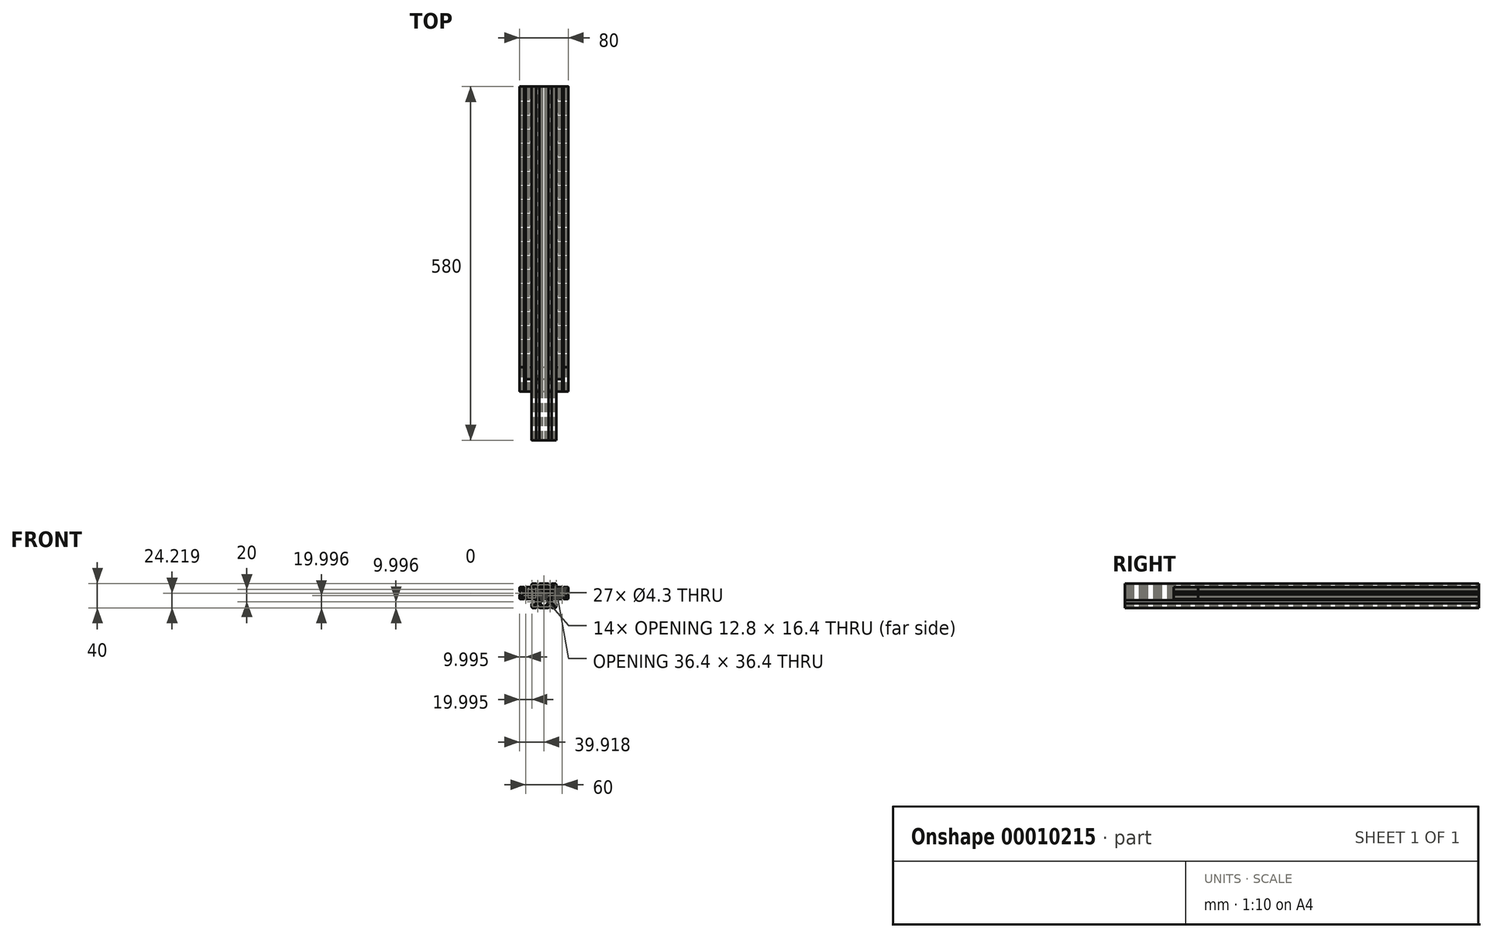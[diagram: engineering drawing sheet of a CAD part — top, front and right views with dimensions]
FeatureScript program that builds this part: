
annotation { "Feature Type Name" : "Feature", "Feature Type Description" : "" }
export const myFeature = defineFeature(function(context is Context, id is Id, definition is map)
    precondition{}
    {
        {
            var Q0;
            Q0=qCreatedBy(makeId("Front.planeOp"),FACE);
            var sketch = newSketch(context, id + "F0", { "sketchPlane" : qUnion([Q0])});
            skArc(sketch, "E0.0", {"start": v(-8.5, 10) * mm, "mid": v(-9.56, 9.56) * mm, "end": v(-10, 8.5) * mm});
            skLineSegment(sketch, "E1.0", {"start": v(-10, 8.5) * mm, "end": v(-10, 3) * mm});
            skArc(sketch, "E2.0", {"start": v(-2.5, 9.5) * mm, "mid": v(-2.65, 9.85) * mm, "end": v(-3, 10) * mm});
            skLineSegment(sketch, "E3.0", {"start": v(-2.5, 9.5) * mm, "end": v(-2.5, 8.45) * mm});
            skLineSegment(sketch, "E4.0", {"start": v(-2.75, 8.2) * mm, "end": v(-4.44, 8.2) * mm});
            skArc(sketch, "E5.0", {"start": v(-4.44, 8.2) * mm, "mid": v(-5.46, 7.52) * mm, "end": v(-5.22, 6.32) * mm});
            skLineSegment(sketch, "E6.0", {"start": v(-2.94, 4.04) * mm, "end": v(-5.22, 6.32) * mm});
            skArc(sketch, "E7.0", {"start": v(-2.94, 4.04) * mm, "mid": v(-2.45, 3.71) * mm, "end": v(-1.88, 3.6) * mm});
            skLineSegment(sketch, "E8.0", {"start": v(-1.88, 3.6) * mm, "end": v(1.88, 3.6) * mm});
            skArc(sketch, "E9.0", {"start": v(1.88, 3.6) * mm, "mid": v(2.45, 3.71) * mm, "end": v(2.94, 4.04) * mm});
            skLineSegment(sketch, "E10.0", {"start": v(2.94, 4.04) * mm, "end": v(5.22, 6.32) * mm});
            skArc(sketch, "E11.0", {"start": v(5.22, 6.32) * mm, "mid": v(5.46, 7.52) * mm, "end": v(4.44, 8.2) * mm});
            skLineSegment(sketch, "E12.0", {"start": v(4.44, 8.2) * mm, "end": v(2.75, 8.2) * mm});
            skArc(sketch, "E13.0", {"start": v(3, 10) * mm, "mid": v(2.65, 9.85) * mm, "end": v(2.5, 9.5) * mm});
            skLineSegment(sketch, "E14.0", {"start": v(3, 10) * mm, "end": v(8.5, 10) * mm});
            skArc(sketch, "E15.0", {"start": v(10, 8.5) * mm, "mid": v(9.56, 9.56) * mm, "end": v(8.5, 10) * mm});
            skLineSegment(sketch, "E16.0", {"start": v(10, 8.5) * mm, "end": v(10, 3) * mm});
            skArc(sketch, "E17.0", {"start": v(9.5, 2.5) * mm, "mid": v(9.85, 2.65) * mm, "end": v(10, 3) * mm});
            skLineSegment(sketch, "E18.0", {"start": v(8.45, 2.5) * mm, "end": v(9.5, 2.5) * mm});
            skLineSegment(sketch, "E19.0", {"start": v(-8.5, 10) * mm, "end": v(-3, 10) * mm});
            skArc(sketch, "E20.0", {"start": v(-10, 3) * mm, "mid": v(-9.85, 2.65) * mm, "end": v(-9.5, 2.5) * mm});
            skLineSegment(sketch, "E21.0", {"start": v(-8.45, 2.5) * mm, "end": v(-9.5, 2.5) * mm});
            skArc(sketch, "E22.0", {"start": v(-8.45, 2.5) * mm, "mid": v(-8.27, 2.57) * mm, "end": v(-8.2, 2.75) * mm});
            skLineSegment(sketch, "E22.1", {"start": v(-8.2, 4.44) * mm, "end": v(-8.2, 2.75) * mm});
            skArc(sketch, "E22.2", {"start": v(-6.32, 5.22) * mm, "mid": v(-7.52, 5.46) * mm, "end": v(-8.2, 4.44) * mm});
            skLineSegment(sketch, "E23.0", {"start": v(-4.04, 2.94) * mm, "end": v(-6.32, 5.22) * mm});
            skArc(sketch, "E24.0", {"start": v(-3.6, 1.88) * mm, "mid": v(-3.71, 2.45) * mm, "end": v(-4.04, 2.94) * mm});
            skLineSegment(sketch, "E25.0", {"start": v(-3.6, 1.88) * mm, "end": v(-3.6, -1.88) * mm});
            skArc(sketch, "E26.0", {"start": v(-4.04, -2.94) * mm, "mid": v(-3.71, -2.45) * mm, "end": v(-3.6, -1.88) * mm});
            skLineSegment(sketch, "E27.0", {"start": v(-4.04, -2.94) * mm, "end": v(-6.32, -5.22) * mm});
            skArc(sketch, "E28.0", {"start": v(-8.2, -4.44) * mm, "mid": v(-7.52, -5.46) * mm, "end": v(-6.32, -5.22) * mm});
            skLineSegment(sketch, "E29.0", {"start": v(-8.2, -2.75) * mm, "end": v(-8.2, -4.44) * mm});
            skArc(sketch, "E30.0", {"start": v(-8.2, -2.75) * mm, "mid": v(-8.27, -2.57) * mm, "end": v(-8.45, -2.5) * mm});
            skLineSegment(sketch, "E31.0", {"start": v(-8.45, -2.5) * mm, "end": v(-9.5, -2.5) * mm});
            skArc(sketch, "E32.0", {"start": v(-9.5, -2.5) * mm, "mid": v(-9.85, -2.65) * mm, "end": v(-10, -3) * mm});
            skLineSegment(sketch, "E33.0", {"start": v(-10, -3) * mm, "end": v(-10, -8.5) * mm});
            skArc(sketch, "E34.0", {"start": v(-10, -8.5) * mm, "mid": v(-9.56, -9.56) * mm, "end": v(-8.5, -10) * mm});
            skLineSegment(sketch, "E35.0", {"start": v(-8.5, -10) * mm, "end": v(-3, -10) * mm});
            skArc(sketch, "E36.0", {"start": v(-3, -10) * mm, "mid": v(-2.65, -9.85) * mm, "end": v(-2.5, -9.5) * mm});
            skLineSegment(sketch, "E37.0", {"start": v(-2.5, -9.5) * mm, "end": v(-2.5, -8.45) * mm});
            skArc(sketch, "E38.0", {"start": v(-2.5, -8.45) * mm, "mid": v(-2.57, -8.27) * mm, "end": v(-2.75, -8.2) * mm});
            skLineSegment(sketch, "E39.0", {"start": v(-4.44, -8.2) * mm, "end": v(-2.75, -8.2) * mm});
            skArc(sketch, "E40.0", {"start": v(-5.22, -6.32) * mm, "mid": v(-5.46, -7.52) * mm, "end": v(-4.44, -8.2) * mm});
            skLineSegment(sketch, "E41.0", {"start": v(-2.94, -4.04) * mm, "end": v(-5.22, -6.32) * mm});
            skArc(sketch, "E42.0", {"start": v(-1.88, -3.6) * mm, "mid": v(-2.45, -3.71) * mm, "end": v(-2.94, -4.04) * mm});
            skLineSegment(sketch, "E43.0", {"start": v(-1.88, -3.6) * mm, "end": v(1.88, -3.6) * mm});
            skArc(sketch, "E44.0", {"start": v(2.94, -4.04) * mm, "mid": v(2.45, -3.71) * mm, "end": v(1.88, -3.6) * mm});
            skLineSegment(sketch, "E45.0", {"start": v(2.94, -4.04) * mm, "end": v(5.22, -6.32) * mm});
            skArc(sketch, "E46.0", {"start": v(4.44, -8.2) * mm, "mid": v(5.46, -7.52) * mm, "end": v(5.22, -6.32) * mm});
            skLineSegment(sketch, "E47.0", {"start": v(2.75, -8.2) * mm, "end": v(4.44, -8.2) * mm});
            skArc(sketch, "E48.0", {"start": v(2.75, -8.2) * mm, "mid": v(2.57, -8.27) * mm, "end": v(2.5, -8.45) * mm});
            skLineSegment(sketch, "E49.0", {"start": v(2.5, -9.5) * mm, "end": v(2.5, -8.45) * mm});
            skArc(sketch, "E50.0", {"start": v(2.5, -9.5) * mm, "mid": v(2.65, -9.85) * mm, "end": v(3, -10) * mm});
            skLineSegment(sketch, "E51.0", {"start": v(3, -10) * mm, "end": v(8.5, -10) * mm});
            skArc(sketch, "E52.0", {"start": v(8.5, -10) * mm, "mid": v(9.56, -9.56) * mm, "end": v(10, -8.5) * mm});
            skLineSegment(sketch, "E53.0", {"start": v(10, -3) * mm, "end": v(10, -8.5) * mm});
            skArc(sketch, "E54.0", {"start": v(10, -3) * mm, "mid": v(9.85, -2.65) * mm, "end": v(9.5, -2.5) * mm});
            skLineSegment(sketch, "E55.0", {"start": v(8.45, -2.5) * mm, "end": v(9.5, -2.5) * mm});
            skArc(sketch, "E56.0", {"start": v(8.45, -2.5) * mm, "mid": v(8.27, -2.57) * mm, "end": v(8.2, -2.75) * mm});
            skLineSegment(sketch, "E57.0", {"start": v(8.2, -4.44) * mm, "end": v(8.2, -2.75) * mm});
            skArc(sketch, "E58.0", {"start": v(6.32, -5.22) * mm, "mid": v(7.52, -5.46) * mm, "end": v(8.2, -4.44) * mm});
            skLineSegment(sketch, "E59.0", {"start": v(4.04, -2.94) * mm, "end": v(6.32, -5.22) * mm});
            skArc(sketch, "E60.0", {"start": v(3.6, -1.88) * mm, "mid": v(3.71, -2.45) * mm, "end": v(4.04, -2.94) * mm});
            skLineSegment(sketch, "E61.0", {"start": v(3.6, 1.88) * mm, "end": v(3.6, -1.88) * mm});
            skArc(sketch, "E62.0", {"start": v(4.04, 2.94) * mm, "mid": v(3.71, 2.45) * mm, "end": v(3.6, 1.88) * mm});
            skLineSegment(sketch, "E63.0", {"start": v(4.04, 2.94) * mm, "end": v(6.32, 5.22) * mm});
            skArc(sketch, "E64.0", {"start": v(8.2, 4.44) * mm, "mid": v(7.52, 5.46) * mm, "end": v(6.32, 5.22) * mm});
            skLineSegment(sketch, "E65.0", {"start": v(8.2, 2.75) * mm, "end": v(8.2, 4.44) * mm});
            skArc(sketch, "E66.0", {"start": v(8.2, 2.75) * mm, "mid": v(8.27, 2.57) * mm, "end": v(8.45, 2.5) * mm});
            skLineSegment(sketch, "E67.0", {"start": v(2.5, 9.5) * mm, "end": v(2.5, 8.45) * mm});
            skArc(sketch, "E68.0", {"start": v(2.5, 8.45) * mm, "mid": v(2.57, 8.27) * mm, "end": v(2.75, 8.2) * mm});
            skArc(sketch, "E69.0", {"start": v(-2.75, 8.2) * mm, "mid": v(-2.57, 8.27) * mm, "end": v(-2.5, 8.45) * mm});
            skCircle(sketch, "E70.0", {"center": v(0, 0) * mm, "radius": 2.15 * mm});
            skSolve(sketch);
        }
        {
            var Q0;
            Q0=qCreatedBy(makeId("Front.planeOp"),FACE);
            var sketch = newSketch(context, id + "F1", { "sketchPlane" : qUnion([Q0])});
            skArc(sketch, "E71.0", {"start": v(-18.5, 10) * mm, "mid": v(-19.56, 9.56) * mm, "end": v(-20, 8.5) * mm});
            skLineSegment(sketch, "E72.0", {"start": v(-18.5, 10) * mm, "end": v(-13, 10) * mm});
            skArc(sketch, "E73.0", {"start": v(-12.5, 9.5) * mm, "mid": v(-12.65, 9.85) * mm, "end": v(-13, 10) * mm});
            skLineSegment(sketch, "E74.0", {"start": v(-12.5, 9.5) * mm, "end": v(-12.5, 8.45) * mm});
            skArc(sketch, "E75.0", {"start": v(-12.75, 8.2) * mm, "mid": v(-12.57, 8.27) * mm, "end": v(-12.5, 8.45) * mm});
            skLineSegment(sketch, "E76.0", {"start": v(-12.75, 8.2) * mm, "end": v(-14.44, 8.2) * mm});
            skArc(sketch, "E77.0", {"start": v(-14.44, 8.2) * mm, "mid": v(-15.46, 7.52) * mm, "end": v(-15.22, 6.32) * mm});
            skLineSegment(sketch, "E78.0", {"start": v(-12.94, 4.04) * mm, "end": v(-15.22, 6.32) * mm});
            skArc(sketch, "E79.0", {"start": v(-12.94, 4.04) * mm, "mid": v(-12.45, 3.71) * mm, "end": v(-11.88, 3.6) * mm});
            skLineSegment(sketch, "E80.0", {"start": v(-11.88, 3.6) * mm, "end": v(-8.12, 3.6) * mm});
            skArc(sketch, "E81.0", {"start": v(-8.12, 3.6) * mm, "mid": v(-7.55, 3.71) * mm, "end": v(-7.06, 4.04) * mm});
            skLineSegment(sketch, "E82.0", {"start": v(-7.06, 4.04) * mm, "end": v(-4.78, 6.32) * mm});
            skArc(sketch, "E83.0", {"start": v(-4.78, 6.32) * mm, "mid": v(-4.54, 7.52) * mm, "end": v(-5.56, 8.2) * mm});
            skLineSegment(sketch, "E84.0", {"start": v(-5.56, 8.2) * mm, "end": v(-7.25, 8.2) * mm});
            skArc(sketch, "E85.0", {"start": v(-7.5, 8.45) * mm, "mid": v(-7.43, 8.27) * mm, "end": v(-7.25, 8.2) * mm});
            skLineSegment(sketch, "E86.0", {"start": v(-7.5, 9.5) * mm, "end": v(-7.5, 8.45) * mm});
            skArc(sketch, "E87.0", {"start": v(-7, 10) * mm, "mid": v(-7.35, 9.85) * mm, "end": v(-7.5, 9.5) * mm});
            skLineSegment(sketch, "E88.0", {"start": v(-20, 8.5) * mm, "end": v(-20, 3) * mm});
            skArc(sketch, "E89.0", {"start": v(-20, 3) * mm, "mid": v(-19.85, 2.65) * mm, "end": v(-19.5, 2.5) * mm});
            skLineSegment(sketch, "E90.0", {"start": v(-18.45, 2.5) * mm, "end": v(-19.5, 2.5) * mm});
            skArc(sketch, "E91.0", {"start": v(-18.45, 2.5) * mm, "mid": v(-18.27, 2.57) * mm, "end": v(-18.2, 2.75) * mm});
            skLineSegment(sketch, "E92.0", {"start": v(-18.2, 4.44) * mm, "end": v(-18.2, 2.75) * mm});
            skArc(sketch, "E93.0", {"start": v(-16.32, 5.22) * mm, "mid": v(-17.52, 5.46) * mm, "end": v(-18.2, 4.44) * mm});
            skLineSegment(sketch, "E94.0", {"start": v(-14.04, 2.94) * mm, "end": v(-16.32, 5.22) * mm});
            skArc(sketch, "E95.0", {"start": v(-13.6, 1.88) * mm, "mid": v(-13.71, 2.45) * mm, "end": v(-14.04, 2.94) * mm});
            skLineSegment(sketch, "E96.0", {"start": v(-13.6, 1.88) * mm, "end": v(-13.6, -1.88) * mm});
            skArc(sketch, "E97.0", {"start": v(-14.04, -2.94) * mm, "mid": v(-13.71, -2.45) * mm, "end": v(-13.6, -1.88) * mm});
            skLineSegment(sketch, "E98.0", {"start": v(-14.04, -2.94) * mm, "end": v(-16.32, -5.22) * mm});
            skArc(sketch, "E99.0", {"start": v(-18.2, -4.44) * mm, "mid": v(-17.52, -5.46) * mm, "end": v(-16.32, -5.22) * mm});
            skLineSegment(sketch, "E100.0", {"start": v(-18.2, -2.75) * mm, "end": v(-18.2, -4.44) * mm});
            skArc(sketch, "E101.0", {"start": v(-18.2, -2.75) * mm, "mid": v(-18.27, -2.57) * mm, "end": v(-18.45, -2.5) * mm});
            skLineSegment(sketch, "E102.0", {"start": v(-18.45, -2.5) * mm, "end": v(-19.5, -2.5) * mm});
            skArc(sketch, "E103.0", {"start": v(-19.5, -2.5) * mm, "mid": v(-19.85, -2.65) * mm, "end": v(-20, -3) * mm});
            skLineSegment(sketch, "E104.0", {"start": v(-20, -3) * mm, "end": v(-20, -8.5) * mm});
            skArc(sketch, "E105.0", {"start": v(-20, -8.5) * mm, "mid": v(-19.56, -9.56) * mm, "end": v(-18.5, -10) * mm});
            skLineSegment(sketch, "E106.0", {"start": v(-18.5, -10) * mm, "end": v(-13, -10) * mm});
            skArc(sketch, "E107.0", {"start": v(-13, -10) * mm, "mid": v(-12.65, -9.85) * mm, "end": v(-12.5, -9.5) * mm});
            skLineSegment(sketch, "E108.0", {"start": v(-12.5, -9.5) * mm, "end": v(-12.5, -8.45) * mm});
            skArc(sketch, "E109.0", {"start": v(-12.5, -8.45) * mm, "mid": v(-12.57, -8.27) * mm, "end": v(-12.75, -8.2) * mm});
            skLineSegment(sketch, "E110.0", {"start": v(-14.44, -8.2) * mm, "end": v(-12.75, -8.2) * mm});
            skArc(sketch, "E111.0", {"start": v(-15.22, -6.32) * mm, "mid": v(-15.46, -7.52) * mm, "end": v(-14.44, -8.2) * mm});
            skLineSegment(sketch, "E112.0", {"start": v(-12.94, -4.04) * mm, "end": v(-15.22, -6.32) * mm});
            skArc(sketch, "E113.0", {"start": v(-11.88, -3.6) * mm, "mid": v(-12.45, -3.71) * mm, "end": v(-12.94, -4.04) * mm});
            skLineSegment(sketch, "E114.0", {"start": v(-11.88, -3.6) * mm, "end": v(-8.12, -3.6) * mm});
            skArc(sketch, "E115.0", {"start": v(-7.06, -4.04) * mm, "mid": v(-7.55, -3.71) * mm, "end": v(-8.12, -3.6) * mm});
            skCircle(sketch, "E116.0", {"center": v(-10, 0) * mm, "radius": 2.15 * mm});
            skLineSegment(sketch, "E117.0", {"start": v(-7.06, -4.04) * mm, "end": v(-4.78, -6.32) * mm});
            skArc(sketch, "E118.0", {"start": v(-5.56, -8.2) * mm, "mid": v(-4.54, -7.52) * mm, "end": v(-4.78, -6.32) * mm});
            skLineSegment(sketch, "E119.0", {"start": v(-7.25, -8.2) * mm, "end": v(-5.56, -8.2) * mm});
            skArc(sketch, "E120.0", {"start": v(-7.25, -8.2) * mm, "mid": v(-7.43, -8.27) * mm, "end": v(-7.5, -8.45) * mm});
            skLineSegment(sketch, "E121.0", {"start": v(-7.5, -9.5) * mm, "end": v(-7.5, -8.45) * mm});
            skArc(sketch, "E122.0", {"start": v(-7.5, -9.5) * mm, "mid": v(-7.35, -9.85) * mm, "end": v(-7, -10) * mm});
            skArc(sketch, "E123.0", {"start": v(-5.96, 2.94) * mm, "mid": v(-6.29, 2.45) * mm, "end": v(-6.4, 1.88) * mm});
            skLineSegment(sketch, "E124.0", {"start": v(-6.4, 1.88) * mm, "end": v(-6.4, -1.88) * mm});
            skArc(sketch, "E125.0", {"start": v(-6.4, -1.88) * mm, "mid": v(-6.29, -2.45) * mm, "end": v(-5.96, -2.94) * mm});
            skArc(sketch, "E126.0", {"start": v(-0.08, 8.2) * mm, "mid": v(-0.65, 8.09) * mm, "end": v(-1.14, 7.76) * mm});
            skArc(sketch, "E127.0", {"start": v(1.14, 7.76) * mm, "mid": v(0.65, 8.09) * mm, "end": v(0.08, 8.2) * mm});
            skArc(sketch, "E128.0", {"start": v(5.96, 2.94) * mm, "mid": v(6.29, 2.45) * mm, "end": v(6.4, 1.88) * mm});
            skLineSegment(sketch, "E129.0", {"start": v(6.4, 1.88) * mm, "end": v(6.4, -1.88) * mm});
            skArc(sketch, "E130.0", {"start": v(6.4, -1.88) * mm, "mid": v(6.29, -2.45) * mm, "end": v(5.96, -2.94) * mm});
            skArc(sketch, "E131.0", {"start": v(-1.14, -7.76) * mm, "mid": v(-0.65, -8.09) * mm, "end": v(-0.08, -8.2) * mm});
            skArc(sketch, "E132.0", {"start": v(0.08, -8.2) * mm, "mid": v(0.65, -8.09) * mm, "end": v(1.14, -7.76) * mm});
            skLineSegment(sketch, "E133.0", {"start": v(0.08, -8.2) * mm, "end": v(-0.08, -8.2) * mm});
            skLineSegment(sketch, "E134.0", {"start": v(0.08, 8.2) * mm, "end": v(-0.08, 8.2) * mm});
            skArc(sketch, "E135.0", {"start": v(7, 10) * mm, "mid": v(7.35, 9.85) * mm, "end": v(7.5, 9.5) * mm});
            skLineSegment(sketch, "E136.0", {"start": v(7.5, 9.5) * mm, "end": v(7.5, 8.45) * mm});
            skArc(sketch, "E137.0", {"start": v(7.5, 8.45) * mm, "mid": v(7.43, 8.27) * mm, "end": v(7.25, 8.2) * mm});
            skLineSegment(sketch, "E138.0", {"start": v(5.56, 8.2) * mm, "end": v(7.25, 8.2) * mm});
            skArc(sketch, "E139.0", {"start": v(4.78, 6.32) * mm, "mid": v(4.54, 7.52) * mm, "end": v(5.56, 8.2) * mm});
            skLineSegment(sketch, "E140.0", {"start": v(7.06, 4.04) * mm, "end": v(4.78, 6.32) * mm});
            skArc(sketch, "E141.0", {"start": v(8.12, 3.6) * mm, "mid": v(7.55, 3.71) * mm, "end": v(7.06, 4.04) * mm});
            skLineSegment(sketch, "E142.0", {"start": v(11.88, 3.6) * mm, "end": v(8.12, 3.6) * mm});
            skArc(sketch, "E143.0", {"start": v(12.94, 4.04) * mm, "mid": v(12.45, 3.71) * mm, "end": v(11.88, 3.6) * mm});
            skLineSegment(sketch, "E144.0", {"start": v(12.94, 4.04) * mm, "end": v(15.22, 6.32) * mm});
            skArc(sketch, "E145.0", {"start": v(14.44, 8.2) * mm, "mid": v(15.46, 7.52) * mm, "end": v(15.22, 6.32) * mm});
            skLineSegment(sketch, "E146.0", {"start": v(12.75, 8.2) * mm, "end": v(14.44, 8.2) * mm});
            skArc(sketch, "E147.0", {"start": v(12.75, 8.2) * mm, "mid": v(12.57, 8.27) * mm, "end": v(12.5, 8.45) * mm});
            skLineSegment(sketch, "E148.0", {"start": v(12.5, 9.5) * mm, "end": v(12.5, 8.45) * mm});
            skArc(sketch, "E149.0", {"start": v(12.5, 9.5) * mm, "mid": v(12.65, 9.85) * mm, "end": v(13, 10) * mm});
            skLineSegment(sketch, "E150.0", {"start": v(18.5, 10) * mm, "end": v(13, 10) * mm});
            skArc(sketch, "E151.0", {"start": v(18.5, 10) * mm, "mid": v(19.56, 9.56) * mm, "end": v(20, 8.5) * mm});
            skLineSegment(sketch, "E152.0", {"start": v(20, 8.5) * mm, "end": v(20, 3) * mm});
            skArc(sketch, "E153.0", {"start": v(20, 3) * mm, "mid": v(19.85, 2.65) * mm, "end": v(19.5, 2.5) * mm});
            skLineSegment(sketch, "E154.0", {"start": v(18.45, 2.5) * mm, "end": v(19.5, 2.5) * mm});
            skArc(sketch, "E155.0", {"start": v(18.45, 2.5) * mm, "mid": v(18.27, 2.57) * mm, "end": v(18.2, 2.75) * mm});
            skLineSegment(sketch, "E156.0", {"start": v(18.2, 4.44) * mm, "end": v(18.2, 2.75) * mm});
            skArc(sketch, "E157.0", {"start": v(16.32, 5.22) * mm, "mid": v(17.52, 5.46) * mm, "end": v(18.2, 4.44) * mm});
            skLineSegment(sketch, "E158.0", {"start": v(14.04, 2.94) * mm, "end": v(16.32, 5.22) * mm});
            skArc(sketch, "E159.0", {"start": v(13.6, 1.88) * mm, "mid": v(13.71, 2.45) * mm, "end": v(14.04, 2.94) * mm});
            skLineSegment(sketch, "E160.0", {"start": v(13.6, 1.88) * mm, "end": v(13.6, -1.88) * mm});
            skCircle(sketch, "E161.0", {"center": v(10, 0) * mm, "radius": 2.15 * mm});
            skArc(sketch, "E162.0", {"start": v(14.04, -2.94) * mm, "mid": v(13.71, -2.45) * mm, "end": v(13.6, -1.88) * mm});
            skLineSegment(sketch, "E163.0", {"start": v(14.04, -2.94) * mm, "end": v(16.32, -5.22) * mm});
            skArc(sketch, "E164.0", {"start": v(18.2, -4.44) * mm, "mid": v(17.52, -5.46) * mm, "end": v(16.32, -5.22) * mm});
            skLineSegment(sketch, "E165.0", {"start": v(18.2, -2.75) * mm, "end": v(18.2, -4.44) * mm});
            skArc(sketch, "E166.0", {"start": v(18.2, -2.75) * mm, "mid": v(18.27, -2.57) * mm, "end": v(18.45, -2.5) * mm});
            skLineSegment(sketch, "E167.0", {"start": v(18.45, -2.5) * mm, "end": v(19.5, -2.5) * mm});
            skArc(sketch, "E168.0", {"start": v(19.5, -2.5) * mm, "mid": v(19.85, -2.65) * mm, "end": v(20, -3) * mm});
            skLineSegment(sketch, "E169.0", {"start": v(20, -3) * mm, "end": v(20, -8.5) * mm});
            skArc(sketch, "E170.0", {"start": v(20, -8.5) * mm, "mid": v(19.56, -9.56) * mm, "end": v(18.5, -10) * mm});
            skLineSegment(sketch, "E171.0", {"start": v(18.5, -10) * mm, "end": v(13, -10) * mm});
            skArc(sketch, "E172.0", {"start": v(13, -10) * mm, "mid": v(12.65, -9.85) * mm, "end": v(12.5, -9.5) * mm});
            skLineSegment(sketch, "E173.0", {"start": v(12.5, -9.5) * mm, "end": v(12.5, -8.45) * mm});
            skArc(sketch, "E174.0", {"start": v(12.5, -8.45) * mm, "mid": v(12.57, -8.27) * mm, "end": v(12.75, -8.2) * mm});
            skLineSegment(sketch, "E175.0", {"start": v(14.44, -8.2) * mm, "end": v(12.75, -8.2) * mm});
            skArc(sketch, "E176.0", {"start": v(15.22, -6.32) * mm, "mid": v(15.46, -7.52) * mm, "end": v(14.44, -8.2) * mm});
            skLineSegment(sketch, "E177.0", {"start": v(12.94, -4.04) * mm, "end": v(15.22, -6.32) * mm});
            skArc(sketch, "E178.0", {"start": v(11.88, -3.6) * mm, "mid": v(12.45, -3.71) * mm, "end": v(12.94, -4.04) * mm});
            skLineSegment(sketch, "E179.0", {"start": v(11.88, -3.6) * mm, "end": v(8.12, -3.6) * mm});
            skArc(sketch, "E180.0", {"start": v(7.06, -4.04) * mm, "mid": v(7.55, -3.71) * mm, "end": v(8.12, -3.6) * mm});
            skLineSegment(sketch, "E181.0", {"start": v(7.06, -4.04) * mm, "end": v(4.78, -6.32) * mm});
            skArc(sketch, "E182.0", {"start": v(5.56, -8.2) * mm, "mid": v(4.54, -7.52) * mm, "end": v(4.78, -6.32) * mm});
            skLineSegment(sketch, "E183.0", {"start": v(7.25, -8.2) * mm, "end": v(5.56, -8.2) * mm});
            skArc(sketch, "E184.0", {"start": v(7.25, -8.2) * mm, "mid": v(7.43, -8.27) * mm, "end": v(7.5, -8.45) * mm});
            skLineSegment(sketch, "E185.0", {"start": v(7.5, -9.5) * mm, "end": v(7.5, -8.45) * mm});
            skArc(sketch, "E186.0", {"start": v(7.5, -9.5) * mm, "mid": v(7.35, -9.85) * mm, "end": v(7, -10) * mm});
            skLineSegment(sketch, "E187", {"start": v(-7, 10) * mm, "end": v(7, 10) * mm});
            skLineSegment(sketch, "E188", {"start": v(-5.96, 2.94) * mm, "end": v(-1.14, 7.76) * mm});
            skLineSegment(sketch, "E189", {"start": v(1.14, 7.76) * mm, "end": v(5.96, 2.94) * mm});
            skLineSegment(sketch, "E190", {"start": v(5.96, -2.94) * mm, "end": v(1.14, -7.76) * mm});
            skLineSegment(sketch, "E191", {"start": v(-1.14, -7.76) * mm, "end": v(-5.96, -2.94) * mm});
            skLineSegment(sketch, "E192", {"start": v(-7, -10) * mm, "end": v(7, -10) * mm});
            skSolve(sketch);
        }
        {
            var Q0;
            Q0=qCreatedBy(makeId("Front.planeOp"),FACE);
            var sketch = newSketch(context, id + "F2", { "sketchPlane" : qUnion([Q0])});
            skLineSegment(sketch, "E193.0.0", {"start": v(-23.1, 10.08) * mm, "end": v(-28.6, 10.08) * mm});
            skArc(sketch, "E193.0.1", {"start": v(-28.6, 10.08) * mm, "mid": v(-29.65, 9.64) * mm, "end": v(-30.1, 8.58) * mm});
            skLineSegment(sketch, "E193.0.2", {"start": v(-30.1, 8.58) * mm, "end": v(-30.1, 3.08) * mm});
            skArc(sketch, "E193.0.3", {"start": v(-30.1, 3.08) * mm, "mid": v(-29.94, 2.72) * mm, "end": v(-29.6, 2.58) * mm});
            skLineSegment(sketch, "E193.0.4", {"start": v(-29.6, 2.58) * mm, "end": v(-28.54, 2.58) * mm});
            skArc(sketch, "E193.0.5", {"start": v(-28.54, 2.58) * mm, "mid": v(-28.36, 2.65) * mm, "end": v(-28.3, 2.83) * mm});
            skLineSegment(sketch, "E193.0.6", {"start": v(-28.3, 2.83) * mm, "end": v(-28.3, 4.52) * mm});
            skArc(sketch, "E193.0.7", {"start": v(-28.3, 4.52) * mm, "mid": v(-27.61, 5.54) * mm, "end": v(-26.41, 5.3) * mm});
            skLineSegment(sketch, "E193.0.8", {"start": v(-26.41, 5.3) * mm, "end": v(-24.13, 3.02) * mm});
            skArc(sketch, "E193.0.9", {"start": v(-24.13, 3.02) * mm, "mid": v(-23.8, 2.53) * mm, "end": v(-23.7, 1.96) * mm});
            skLineSegment(sketch, "E193.0.10", {"start": v(-23.7, 1.96) * mm, "end": v(-23.7, -1.8) * mm});
            skArc(sketch, "E193.0.11", {"start": v(-23.7, -1.8) * mm, "mid": v(-23.8, -2.37) * mm, "end": v(-24.13, -2.86) * mm});
            skLineSegment(sketch, "E193.0.12", {"start": v(-24.13, -2.86) * mm, "end": v(-26.41, -5.14) * mm});
            skArc(sketch, "E193.0.13", {"start": v(-26.41, -5.14) * mm, "mid": v(-27.61, -5.38) * mm, "end": v(-28.3, -4.37) * mm});
            skLineSegment(sketch, "E193.0.14", {"start": v(-28.3, -4.37) * mm, "end": v(-28.3, -2.67) * mm});
            skArc(sketch, "E193.0.15", {"start": v(-28.3, -2.67) * mm, "mid": v(-28.36, -2.5) * mm, "end": v(-28.54, -2.42) * mm});
            skLineSegment(sketch, "E193.0.16", {"start": v(-28.54, -2.42) * mm, "end": v(-29.6, -2.42) * mm});
            skArc(sketch, "E193.0.17", {"start": v(-29.6, -2.42) * mm, "mid": v(-29.94, -2.57) * mm, "end": v(-30.1, -2.92) * mm});
            skLineSegment(sketch, "E193.0.18", {"start": v(-30.1, -2.92) * mm, "end": v(-30.1, -8.42) * mm});
            skArc(sketch, "E193.0.19", {"start": v(-30.1, -8.42) * mm, "mid": v(-29.65, -9.48) * mm, "end": v(-28.6, -9.92) * mm});
            skLineSegment(sketch, "E193.0.20", {"start": v(-28.6, -9.92) * mm, "end": v(-23.1, -9.92) * mm});
            skArc(sketch, "E193.0.21", {"start": v(-23.1, -9.92) * mm, "mid": v(-22.74, -9.78) * mm, "end": v(-22.6, -9.42) * mm});
            skLineSegment(sketch, "E193.0.22", {"start": v(-22.6, -9.42) * mm, "end": v(-22.6, -8.37) * mm});
            skArc(sketch, "E193.0.23", {"start": v(-22.6, -8.37) * mm, "mid": v(-22.66, -8.2) * mm, "end": v(-22.84, -8.12) * mm});
            skLineSegment(sketch, "E193.0.24", {"start": v(-22.84, -8.12) * mm, "end": v(-24.54, -8.12) * mm});
            skArc(sketch, "E193.0.25", {"start": v(-24.54, -8.12) * mm, "mid": v(-25.55, -7.44) * mm, "end": v(-25.31, -6.24) * mm});
            skLineSegment(sketch, "E193.0.26", {"start": v(-25.31, -6.24) * mm, "end": v(-23.03, -3.96) * mm});
            skArc(sketch, "E193.0.27", {"start": v(-23.03, -3.96) * mm, "mid": v(-22.54, -3.64) * mm, "end": v(-21.97, -3.52) * mm});
            skLineSegment(sketch, "E193.0.28", {"start": v(-21.97, -3.52) * mm, "end": v(-18.21, -3.52) * mm});
            skArc(sketch, "E193.0.29", {"start": v(-18.21, -3.52) * mm, "mid": v(-17.64, -3.64) * mm, "end": v(-17.15, -3.96) * mm});
            skLineSegment(sketch, "E193.0.30", {"start": v(-17.15, -3.96) * mm, "end": v(-14.87, -6.24) * mm});
            skArc(sketch, "E193.0.31", {"start": v(-14.87, -6.24) * mm, "mid": v(-14.63, -7.44) * mm, "end": v(-15.65, -8.12) * mm});
            skLineSegment(sketch, "E193.0.32", {"start": v(-15.65, -8.12) * mm, "end": v(-17.34, -8.12) * mm});
            skArc(sketch, "E193.0.33", {"start": v(-17.34, -8.12) * mm, "mid": v(-17.52, -8.2) * mm, "end": v(-17.6, -8.37) * mm});
            skLineSegment(sketch, "E193.0.34", {"start": v(-17.6, -8.37) * mm, "end": v(-17.6, -9.42) * mm});
            skArc(sketch, "E193.0.35", {"start": v(-17.6, -9.42) * mm, "mid": v(-17.44, -9.78) * mm, "end": v(-17.1, -9.92) * mm});
            skLineSegment(sketch, "E193.0.36", {"start": v(-17.1, -9.92) * mm, "end": v(-3.1, -9.92) * mm});
            skArc(sketch, "E193.0.37", {"start": v(-3.1, -9.92) * mm, "mid": v(-2.74, -9.78) * mm, "end": v(-2.6, -9.42) * mm});
            skLineSegment(sketch, "E193.0.38", {"start": v(-2.6, -9.42) * mm, "end": v(-2.6, -8.37) * mm});
            skArc(sketch, "E193.0.39", {"start": v(-2.6, -8.37) * mm, "mid": v(-2.66, -8.2) * mm, "end": v(-2.84, -8.12) * mm});
            skLineSegment(sketch, "E193.0.40", {"start": v(-2.84, -8.12) * mm, "end": v(-4.54, -8.12) * mm});
            skArc(sketch, "E193.0.41", {"start": v(-4.54, -8.12) * mm, "mid": v(-5.55, -7.44) * mm, "end": v(-5.31, -6.24) * mm});
            skLineSegment(sketch, "E193.0.42", {"start": v(-5.31, -6.24) * mm, "end": v(-3.03, -3.96) * mm});
            skArc(sketch, "E193.0.43", {"start": v(-3.03, -3.96) * mm, "mid": v(-2.54, -3.64) * mm, "end": v(-1.97, -3.52) * mm});
            skLineSegment(sketch, "E193.0.44", {"start": v(-1.97, -3.52) * mm, "end": v(1.79, -3.52) * mm});
            skArc(sketch, "E193.0.45", {"start": v(1.79, -3.52) * mm, "mid": v(2.36, -3.64) * mm, "end": v(2.85, -3.96) * mm});
            skLineSegment(sketch, "E193.0.46", {"start": v(2.85, -3.96) * mm, "end": v(5.13, -6.24) * mm});
            skArc(sketch, "E193.0.47", {"start": v(5.13, -6.24) * mm, "mid": v(5.37, -7.44) * mm, "end": v(4.35, -8.12) * mm});
            skLineSegment(sketch, "E193.0.48", {"start": v(4.35, -8.12) * mm, "end": v(2.66, -8.12) * mm});
            skArc(sketch, "E193.0.49", {"start": v(2.66, -8.12) * mm, "mid": v(2.48, -8.2) * mm, "end": v(2.4, -8.37) * mm});
            skLineSegment(sketch, "E193.0.50", {"start": v(2.4, -8.37) * mm, "end": v(2.4, -9.42) * mm});
            skArc(sketch, "E193.0.51", {"start": v(2.4, -9.42) * mm, "mid": v(2.56, -9.78) * mm, "end": v(2.9, -9.92) * mm});
            skArc(sketch, "E193.0.61", {"start": v(3.95, -2.86) * mm, "mid": v(3.62, -2.37) * mm, "end": v(3.5, -1.8) * mm});
            skLineSegment(sketch, "E193.0.62", {"start": v(3.5, -1.8) * mm, "end": v(3.5, 1.96) * mm});
            skArc(sketch, "E193.0.63", {"start": v(3.5, 1.96) * mm, "mid": v(3.62, 2.53) * mm, "end": v(3.95, 3.02) * mm});
            skArc(sketch, "E193.0.73", {"start": v(2.9, 10.08) * mm, "mid": v(2.56, 9.93) * mm, "end": v(2.4, 9.58) * mm});
            skLineSegment(sketch, "E193.0.74", {"start": v(2.4, 9.58) * mm, "end": v(2.4, 8.53) * mm});
            skArc(sketch, "E193.0.75", {"start": v(2.4, 8.53) * mm, "mid": v(2.48, 8.35) * mm, "end": v(2.66, 8.28) * mm});
            skLineSegment(sketch, "E193.0.76", {"start": v(2.66, 8.28) * mm, "end": v(4.35, 8.28) * mm});
            skArc(sketch, "E193.0.77", {"start": v(4.35, 8.28) * mm, "mid": v(5.37, 7.6) * mm, "end": v(5.13, 6.4) * mm});
            skLineSegment(sketch, "E193.0.78", {"start": v(5.13, 6.4) * mm, "end": v(2.85, 4.12) * mm});
            skArc(sketch, "E193.0.79", {"start": v(2.85, 4.12) * mm, "mid": v(2.36, 3.8) * mm, "end": v(1.79, 3.68) * mm});
            skLineSegment(sketch, "E193.0.80", {"start": v(1.79, 3.68) * mm, "end": v(-1.97, 3.68) * mm});
            skArc(sketch, "E193.0.81", {"start": v(-1.97, 3.68) * mm, "mid": v(-2.54, 3.8) * mm, "end": v(-3.03, 4.12) * mm});
            skLineSegment(sketch, "E193.0.82", {"start": v(-3.03, 4.12) * mm, "end": v(-5.31, 6.4) * mm});
            skArc(sketch, "E193.0.83", {"start": v(-5.31, 6.4) * mm, "mid": v(-5.55, 7.6) * mm, "end": v(-4.54, 8.28) * mm});
            skLineSegment(sketch, "E193.0.84", {"start": v(-4.54, 8.28) * mm, "end": v(-2.84, 8.28) * mm});
            skArc(sketch, "E193.0.85", {"start": v(-2.84, 8.28) * mm, "mid": v(-2.66, 8.35) * mm, "end": v(-2.6, 8.53) * mm});
            skLineSegment(sketch, "E193.0.86", {"start": v(-2.6, 8.53) * mm, "end": v(-2.6, 9.58) * mm});
            skArc(sketch, "E193.0.87", {"start": v(-2.6, 9.58) * mm, "mid": v(-2.74, 9.93) * mm, "end": v(-3.1, 10.08) * mm});
            skLineSegment(sketch, "E193.0.88", {"start": v(-3.1, 10.08) * mm, "end": v(-17.1, 10.08) * mm});
            skArc(sketch, "E193.0.89", {"start": v(-17.1, 10.08) * mm, "mid": v(-17.44, 9.93) * mm, "end": v(-17.6, 9.58) * mm});
            skLineSegment(sketch, "E193.0.90", {"start": v(-17.6, 9.58) * mm, "end": v(-17.6, 8.53) * mm});
            skArc(sketch, "E193.0.91", {"start": v(-17.6, 8.53) * mm, "mid": v(-17.52, 8.35) * mm, "end": v(-17.34, 8.28) * mm});
            skLineSegment(sketch, "E193.0.92", {"start": v(-17.34, 8.28) * mm, "end": v(-15.65, 8.28) * mm});
            skArc(sketch, "E193.0.93", {"start": v(-15.65, 8.28) * mm, "mid": v(-14.63, 7.6) * mm, "end": v(-14.87, 6.4) * mm});
            skLineSegment(sketch, "E193.0.94", {"start": v(-14.87, 6.4) * mm, "end": v(-17.15, 4.12) * mm});
            skArc(sketch, "E193.0.95", {"start": v(-17.15, 4.12) * mm, "mid": v(-17.64, 3.8) * mm, "end": v(-18.21, 3.68) * mm});
            skLineSegment(sketch, "E193.0.96", {"start": v(-18.21, 3.68) * mm, "end": v(-21.97, 3.68) * mm});
            skArc(sketch, "E193.0.97", {"start": v(-21.97, 3.68) * mm, "mid": v(-22.54, 3.8) * mm, "end": v(-23.03, 4.12) * mm});
            skLineSegment(sketch, "E193.0.98", {"start": v(-23.03, 4.12) * mm, "end": v(-25.31, 6.4) * mm});
            skArc(sketch, "E193.0.99", {"start": v(-25.31, 6.4) * mm, "mid": v(-25.55, 7.6) * mm, "end": v(-24.54, 8.28) * mm});
            skLineSegment(sketch, "E193.0.100", {"start": v(-24.54, 8.28) * mm, "end": v(-22.84, 8.28) * mm});
            skArc(sketch, "E193.0.101", {"start": v(-22.84, 8.28) * mm, "mid": v(-22.66, 8.35) * mm, "end": v(-22.6, 8.53) * mm});
            skLineSegment(sketch, "E193.0.102", {"start": v(-22.6, 8.53) * mm, "end": v(-22.6, 9.58) * mm});
            skArc(sketch, "E193.0.103", {"start": v(-22.6, 9.58) * mm, "mid": v(-22.74, 9.93) * mm, "end": v(-23.1, 10.08) * mm});
            skLineSegment(sketch, "E194.0.0", {"start": v(-11.23, 7.84) * mm, "end": v(-16.05, 3.02) * mm});
            skArc(sketch, "E194.0.1", {"start": v(-16.05, 3.02) * mm, "mid": v(-16.38, 2.53) * mm, "end": v(-16.5, 1.96) * mm});
            skLineSegment(sketch, "E194.0.2", {"start": v(-16.5, 1.96) * mm, "end": v(-16.5, -1.8) * mm});
            skArc(sketch, "E194.0.3", {"start": v(-16.5, -1.8) * mm, "mid": v(-16.38, -2.37) * mm, "end": v(-16.05, -2.86) * mm});
            skLineSegment(sketch, "E194.0.4", {"start": v(-16.05, -2.86) * mm, "end": v(-11.23, -7.68) * mm});
            skArc(sketch, "E194.0.5", {"start": v(-11.23, -7.68) * mm, "mid": v(-10.74, -8) * mm, "end": v(-10.17, -8.12) * mm});
            skLineSegment(sketch, "E194.0.6", {"start": v(-10.17, -8.12) * mm, "end": v(-10.01, -8.12) * mm});
            skArc(sketch, "E194.0.7", {"start": v(-10.01, -8.12) * mm, "mid": v(-9.44, -8) * mm, "end": v(-8.95, -7.68) * mm});
            skLineSegment(sketch, "E194.0.8", {"start": v(-8.95, -7.68) * mm, "end": v(-4.13, -2.86) * mm});
            skArc(sketch, "E194.0.9", {"start": v(-4.13, -2.86) * mm, "mid": v(-3.8, -2.37) * mm, "end": v(-3.7, -1.8) * mm});
            skLineSegment(sketch, "E194.0.10", {"start": v(-3.7, -1.8) * mm, "end": v(-3.7, 1.96) * mm});
            skArc(sketch, "E194.0.11", {"start": v(-3.7, 1.96) * mm, "mid": v(-3.8, 2.53) * mm, "end": v(-4.13, 3.02) * mm});
            skLineSegment(sketch, "E194.0.12", {"start": v(-4.13, 3.02) * mm, "end": v(-8.95, 7.84) * mm});
            skArc(sketch, "E194.0.13", {"start": v(-8.95, 7.84) * mm, "mid": v(-9.44, 8.16) * mm, "end": v(-10.01, 8.28) * mm});
            skLineSegment(sketch, "E194.0.14", {"start": v(-10.01, 8.28) * mm, "end": v(-10.17, 8.28) * mm});
            skArc(sketch, "E194.0.15", {"start": v(-10.17, 8.28) * mm, "mid": v(-10.74, 8.16) * mm, "end": v(-11.23, 7.84) * mm});
            skCircle(sketch, "E195.0", {"center": v(-20.1, 0.08) * mm, "radius": 2.15 * mm});
            skCircle(sketch, "E196.0", {"center": v(-0.1, 0.08) * mm, "radius": 2.15 * mm});
            skLineSegment(sketch, "E197", {"start": v(-0.1, 11.8) * mm, "end": v(-0.1, -12) * mm, "construction": true});
            skLineSegment(sketch, "E198.0.MirrorCS", {"start": v(3.95, 3.02) * mm, "end": v(8.77, 7.84) * mm});
            skLineSegment(sketch, "E199.0.MirrorCS", {"start": v(8.77, -7.68) * mm, "end": v(3.95, -2.86) * mm});
            skArc(sketch, "E200.0.MirrorCS", {"start": v(9.83, -8.12) * mm, "mid": v(9.26, -8) * mm, "end": v(8.77, -7.68) * mm});
            skArc(sketch, "E201.0.MirrorCS", {"start": v(8.77, 7.84) * mm, "mid": v(9.26, 8.16) * mm, "end": v(9.83, 8.28) * mm});
            skLineSegment(sketch, "E202.0.MirrorCS", {"start": v(9.83, 8.28) * mm, "end": v(9.99, 8.28) * mm});
            skArc(sketch, "E203.0.MirrorCS", {"start": v(9.99, 8.28) * mm, "mid": v(10.56, 8.16) * mm, "end": v(11.05, 7.84) * mm});
            skLineSegment(sketch, "E204.0.MirrorCS", {"start": v(11.05, 7.84) * mm, "end": v(15.87, 3.02) * mm});
            skArc(sketch, "E205.0.MirrorCS", {"start": v(15.87, 3.02) * mm, "mid": v(16.2, 2.53) * mm, "end": v(16.3, 1.96) * mm});
            skLineSegment(sketch, "E206.0.MirrorCS", {"start": v(16.3, 1.96) * mm, "end": v(16.3, -1.8) * mm});
            skArc(sketch, "E207.0.MirrorCS", {"start": v(16.3, -1.8) * mm, "mid": v(16.2, -2.37) * mm, "end": v(15.87, -2.86) * mm});
            skLineSegment(sketch, "E208.0.MirrorCS", {"start": v(15.87, -2.86) * mm, "end": v(11.05, -7.68) * mm});
            skArc(sketch, "E209.0.MirrorCS", {"start": v(11.05, -7.68) * mm, "mid": v(10.56, -8) * mm, "end": v(9.99, -8.12) * mm});
            skLineSegment(sketch, "E210.0.MirrorCS", {"start": v(9.99, -8.12) * mm, "end": v(9.83, -8.12) * mm});
            skLineSegment(sketch, "E211.0.MirrorCS", {"start": v(16.9, -9.92) * mm, "end": v(2.9, -9.92) * mm});
            skLineSegment(sketch, "E212.0.MirrorCS", {"start": v(2.9, 10.08) * mm, "end": v(16.9, 10.08) * mm});
            skArc(sketch, "E213.0.MirrorCS", {"start": v(16.9, 10.08) * mm, "mid": v(17.26, 9.93) * mm, "end": v(17.4, 9.58) * mm});
            skLineSegment(sketch, "E214.0.MirrorCS", {"start": v(17.4, 9.58) * mm, "end": v(17.4, 8.53) * mm});
            skArc(sketch, "E215.0.MirrorCS", {"start": v(17.4, 8.53) * mm, "mid": v(17.34, 8.35) * mm, "end": v(17.16, 8.28) * mm});
            skLineSegment(sketch, "E216.0.MirrorCS", {"start": v(17.16, 8.28) * mm, "end": v(15.46, 8.28) * mm});
            skArc(sketch, "E217.0.MirrorCS", {"start": v(15.46, 8.28) * mm, "mid": v(14.45, 7.6) * mm, "end": v(14.69, 6.4) * mm});
            skLineSegment(sketch, "E218.0.MirrorCS", {"start": v(14.69, 6.4) * mm, "end": v(16.97, 4.12) * mm});
            skArc(sketch, "E219.0.MirrorCS", {"start": v(16.97, 4.12) * mm, "mid": v(17.46, 3.8) * mm, "end": v(18.03, 3.68) * mm});
            skLineSegment(sketch, "E220.0.MirrorCS", {"start": v(18.03, 3.68) * mm, "end": v(21.79, 3.68) * mm});
            skArc(sketch, "E221.0.MirrorCS", {"start": v(21.79, 3.68) * mm, "mid": v(22.36, 3.8) * mm, "end": v(22.85, 4.12) * mm});
            skLineSegment(sketch, "E222.0.MirrorCS", {"start": v(22.85, 4.12) * mm, "end": v(25.13, 6.4) * mm});
            skArc(sketch, "E223.0.MirrorCS", {"start": v(25.13, 6.4) * mm, "mid": v(25.37, 7.6) * mm, "end": v(24.35, 8.28) * mm});
            skLineSegment(sketch, "E224.0.MirrorCS", {"start": v(24.35, 8.28) * mm, "end": v(22.66, 8.28) * mm});
            skArc(sketch, "E225.0.MirrorCS", {"start": v(22.66, 8.28) * mm, "mid": v(22.48, 8.35) * mm, "end": v(22.4, 8.53) * mm});
            skLineSegment(sketch, "E226.0.MirrorCS", {"start": v(22.4, 8.53) * mm, "end": v(22.4, 9.58) * mm});
            skArc(sketch, "E227.0.MirrorCS", {"start": v(22.4, 9.58) * mm, "mid": v(22.56, 9.93) * mm, "end": v(22.9, 10.08) * mm});
            skLineSegment(sketch, "E228.0.MirrorCS", {"start": v(22.9, 10.08) * mm, "end": v(28.4, 10.08) * mm});
            skArc(sketch, "E229.0.MirrorCS", {"start": v(28.4, 10.08) * mm, "mid": v(29.47, 9.64) * mm, "end": v(29.9, 8.58) * mm});
            skLineSegment(sketch, "E230.0.MirrorCS", {"start": v(29.9, 8.58) * mm, "end": v(29.9, 3.08) * mm});
            skArc(sketch, "E231.0.MirrorCS", {"start": v(29.9, 3.08) * mm, "mid": v(29.76, 2.72) * mm, "end": v(29.4, 2.58) * mm});
            skLineSegment(sketch, "E232.0.MirrorCS", {"start": v(29.4, 2.58) * mm, "end": v(28.36, 2.58) * mm});
            skArc(sketch, "E233.0.MirrorCS", {"start": v(28.36, 2.58) * mm, "mid": v(28.18, 2.65) * mm, "end": v(28.1, 2.83) * mm});
            skLineSegment(sketch, "E234.0.MirrorCS", {"start": v(28.1, 2.83) * mm, "end": v(28.1, 4.52) * mm});
            skArc(sketch, "E235.0.MirrorCS", {"start": v(28.1, 4.52) * mm, "mid": v(27.43, 5.54) * mm, "end": v(26.23, 5.3) * mm});
            skLineSegment(sketch, "E236.0.MirrorCS", {"start": v(26.23, 5.3) * mm, "end": v(23.95, 3.02) * mm});
            skArc(sketch, "E237.0.MirrorCS", {"start": v(23.95, 3.02) * mm, "mid": v(23.62, 2.53) * mm, "end": v(23.5, 1.96) * mm});
            skLineSegment(sketch, "E238.0.MirrorCS", {"start": v(23.5, 1.96) * mm, "end": v(23.5, -1.8) * mm});
            skArc(sketch, "E239.0.MirrorCS", {"start": v(23.5, -1.8) * mm, "mid": v(23.62, -2.37) * mm, "end": v(23.95, -2.86) * mm});
            skLineSegment(sketch, "E240.0.MirrorCS", {"start": v(23.95, -2.86) * mm, "end": v(26.23, -5.14) * mm});
            skArc(sketch, "E241.0.MirrorCS", {"start": v(26.23, -5.14) * mm, "mid": v(27.43, -5.38) * mm, "end": v(28.1, -4.37) * mm});
            skLineSegment(sketch, "E242.0.MirrorCS", {"start": v(28.1, -4.37) * mm, "end": v(28.1, -2.67) * mm});
            skArc(sketch, "E243.0.MirrorCS", {"start": v(28.1, -2.67) * mm, "mid": v(28.18, -2.5) * mm, "end": v(28.36, -2.42) * mm});
            skLineSegment(sketch, "E244.0.MirrorCS", {"start": v(28.36, -2.42) * mm, "end": v(29.4, -2.42) * mm});
            skArc(sketch, "E245.0.MirrorCS", {"start": v(29.4, -2.42) * mm, "mid": v(29.76, -2.57) * mm, "end": v(29.9, -2.92) * mm});
            skLineSegment(sketch, "E246.0.MirrorCS", {"start": v(29.9, -2.92) * mm, "end": v(29.9, -8.42) * mm});
            skArc(sketch, "E247.0.MirrorCS", {"start": v(29.9, -8.42) * mm, "mid": v(29.47, -9.48) * mm, "end": v(28.4, -9.92) * mm});
            skLineSegment(sketch, "E248.0.MirrorCS", {"start": v(28.4, -9.92) * mm, "end": v(22.9, -9.92) * mm});
            skArc(sketch, "E249.0.MirrorCS", {"start": v(22.9, -9.92) * mm, "mid": v(22.56, -9.78) * mm, "end": v(22.4, -9.42) * mm});
            skLineSegment(sketch, "E250.0.MirrorCS", {"start": v(22.4, -9.42) * mm, "end": v(22.4, -8.37) * mm});
            skArc(sketch, "E251.0.MirrorCS", {"start": v(22.4, -8.37) * mm, "mid": v(22.48, -8.2) * mm, "end": v(22.66, -8.12) * mm});
            skLineSegment(sketch, "E252.0.MirrorCS", {"start": v(22.66, -8.12) * mm, "end": v(24.35, -8.12) * mm});
            skArc(sketch, "E253.0.MirrorCS", {"start": v(24.35, -8.12) * mm, "mid": v(25.37, -7.44) * mm, "end": v(25.13, -6.24) * mm});
            skLineSegment(sketch, "E254.0.MirrorCS", {"start": v(25.13, -6.24) * mm, "end": v(22.85, -3.96) * mm});
            skArc(sketch, "E255.0.MirrorCS", {"start": v(22.85, -3.96) * mm, "mid": v(22.36, -3.64) * mm, "end": v(21.79, -3.52) * mm});
            skLineSegment(sketch, "E256.0.MirrorCS", {"start": v(21.79, -3.52) * mm, "end": v(18.03, -3.52) * mm});
            skArc(sketch, "E257.0.MirrorCS", {"start": v(18.03, -3.52) * mm, "mid": v(17.46, -3.64) * mm, "end": v(16.97, -3.96) * mm});
            skLineSegment(sketch, "E258.0.MirrorCS", {"start": v(16.97, -3.96) * mm, "end": v(14.69, -6.24) * mm});
            skArc(sketch, "E259.0.MirrorCS", {"start": v(14.69, -6.24) * mm, "mid": v(14.45, -7.44) * mm, "end": v(15.46, -8.12) * mm});
            skLineSegment(sketch, "E260.0.MirrorCS", {"start": v(15.46, -8.12) * mm, "end": v(17.16, -8.12) * mm});
            skArc(sketch, "E261.0.MirrorCS", {"start": v(17.16, -8.12) * mm, "mid": v(17.34, -8.2) * mm, "end": v(17.4, -8.37) * mm});
            skLineSegment(sketch, "E262.0.MirrorCS", {"start": v(17.4, -8.37) * mm, "end": v(17.4, -9.42) * mm});
            skArc(sketch, "E263.0.MirrorCS", {"start": v(17.4, -9.42) * mm, "mid": v(17.26, -9.78) * mm, "end": v(16.9, -9.92) * mm});
            skCircle(sketch, "E264.0.MirrorC", {"center": v(19.9, 0.08) * mm, "radius": 2.15 * mm});
            skSolve(sketch);
        }
        {
            var Q0;
            Q0=qCreatedBy(makeId("Front.planeOp"),FACE);
            var sketch = newSketch(context, id + "F3", { "sketchPlane" : qUnion([Q0])});
            skLineSegment(sketch, "E265.0.0", {"start": v(-32.95, 10) * mm, "end": v(-38.45, 10) * mm});
            skArc(sketch, "E265.0.1", {"start": v(-38.45, 10) * mm, "mid": v(-39.52, 9.56) * mm, "end": v(-39.95, 8.5) * mm});
            skLineSegment(sketch, "E265.0.2", {"start": v(-39.95, 8.5) * mm, "end": v(-39.95, 3) * mm});
            skArc(sketch, "E265.0.3", {"start": v(-39.95, 3) * mm, "mid": v(-39.8, 2.65) * mm, "end": v(-39.45, 2.5) * mm});
            skLineSegment(sketch, "E265.0.4", {"start": v(-39.45, 2.5) * mm, "end": v(-38.4, 2.5) * mm});
            skArc(sketch, "E265.0.5", {"start": v(-38.4, 2.5) * mm, "mid": v(-38.23, 2.57) * mm, "end": v(-38.15, 2.75) * mm});
            skLineSegment(sketch, "E265.0.6", {"start": v(-38.15, 2.75) * mm, "end": v(-38.15, 4.44) * mm});
            skArc(sketch, "E265.0.7", {"start": v(-38.15, 4.44) * mm, "mid": v(-37.48, 5.46) * mm, "end": v(-36.28, 5.22) * mm});
            skLineSegment(sketch, "E265.0.8", {"start": v(-36.28, 5.22) * mm, "end": v(-34, 2.94) * mm});
            skArc(sketch, "E265.0.9", {"start": v(-34, 2.94) * mm, "mid": v(-33.67, 2.45) * mm, "end": v(-33.55, 1.88) * mm});
            skLineSegment(sketch, "E265.0.10", {"start": v(-33.55, 1.88) * mm, "end": v(-33.55, -1.88) * mm});
            skArc(sketch, "E265.0.11", {"start": v(-33.55, -1.88) * mm, "mid": v(-33.67, -2.45) * mm, "end": v(-34, -2.94) * mm});
            skLineSegment(sketch, "E265.0.12", {"start": v(-34, -2.94) * mm, "end": v(-36.28, -5.22) * mm});
            skArc(sketch, "E265.0.13", {"start": v(-36.28, -5.22) * mm, "mid": v(-37.48, -5.46) * mm, "end": v(-38.15, -4.45) * mm});
            skLineSegment(sketch, "E265.0.14", {"start": v(-38.15, -4.45) * mm, "end": v(-38.15, -2.75) * mm});
            skArc(sketch, "E265.0.15", {"start": v(-38.15, -2.75) * mm, "mid": v(-38.23, -2.57) * mm, "end": v(-38.4, -2.5) * mm});
            skLineSegment(sketch, "E265.0.16", {"start": v(-38.4, -2.5) * mm, "end": v(-39.45, -2.5) * mm});
            skArc(sketch, "E265.0.17", {"start": v(-39.45, -2.5) * mm, "mid": v(-39.8, -2.65) * mm, "end": v(-39.95, -3) * mm});
            skLineSegment(sketch, "E265.0.18", {"start": v(-39.95, -3) * mm, "end": v(-39.95, -8.5) * mm});
            skArc(sketch, "E265.0.19", {"start": v(-39.95, -8.5) * mm, "mid": v(-39.52, -9.56) * mm, "end": v(-38.45, -10) * mm});
            skLineSegment(sketch, "E265.0.20", {"start": v(-38.45, -10) * mm, "end": v(-32.95, -10) * mm});
            skArc(sketch, "E265.0.21", {"start": v(-32.95, -10) * mm, "mid": v(-32.6, -9.85) * mm, "end": v(-32.45, -9.5) * mm});
            skLineSegment(sketch, "E265.0.22", {"start": v(-32.45, -9.5) * mm, "end": v(-32.45, -8.45) * mm});
            skArc(sketch, "E265.0.23", {"start": v(-32.45, -8.45) * mm, "mid": v(-32.53, -8.27) * mm, "end": v(-32.7, -8.2) * mm});
            skLineSegment(sketch, "E265.0.24", {"start": v(-32.7, -8.2) * mm, "end": v(-34.4, -8.2) * mm});
            skArc(sketch, "E265.0.25", {"start": v(-34.4, -8.2) * mm, "mid": v(-35.42, -7.52) * mm, "end": v(-35.18, -6.32) * mm});
            skLineSegment(sketch, "E265.0.26", {"start": v(-35.18, -6.32) * mm, "end": v(-32.9, -4.04) * mm});
            skArc(sketch, "E265.0.27", {"start": v(-32.9, -4.04) * mm, "mid": v(-32.4, -3.72) * mm, "end": v(-31.83, -3.6) * mm});
            skLineSegment(sketch, "E265.0.28", {"start": v(-31.83, -3.6) * mm, "end": v(-28.08, -3.6) * mm});
            skArc(sketch, "E265.0.29", {"start": v(-28.08, -3.6) * mm, "mid": v(-27.5, -3.72) * mm, "end": v(-27.02, -4.04) * mm});
            skLineSegment(sketch, "E265.0.30", {"start": v(-27.02, -4.04) * mm, "end": v(-24.73, -6.32) * mm});
            skArc(sketch, "E265.0.31", {"start": v(-24.73, -6.32) * mm, "mid": v(-24.5, -7.52) * mm, "end": v(-25.51, -8.2) * mm});
            skLineSegment(sketch, "E265.0.32", {"start": v(-25.51, -8.2) * mm, "end": v(-27.2, -8.2) * mm});
            skArc(sketch, "E265.0.33", {"start": v(-27.2, -8.2) * mm, "mid": v(-27.38, -8.27) * mm, "end": v(-27.45, -8.45) * mm});
            skLineSegment(sketch, "E265.0.34", {"start": v(-27.45, -8.45) * mm, "end": v(-27.45, -9.5) * mm});
            skArc(sketch, "E265.0.35", {"start": v(-27.45, -9.5) * mm, "mid": v(-27.3, -9.85) * mm, "end": v(-26.95, -10) * mm});
            skLineSegment(sketch, "E265.0.36", {"start": v(-26.95, -10) * mm, "end": v(-12.95, -10) * mm});
            skArc(sketch, "E265.0.37", {"start": v(-12.95, -10) * mm, "mid": v(-12.6, -9.85) * mm, "end": v(-12.45, -9.5) * mm});
            skLineSegment(sketch, "E265.0.38", {"start": v(-12.45, -9.5) * mm, "end": v(-12.45, -8.45) * mm});
            skArc(sketch, "E265.0.39", {"start": v(-12.45, -8.45) * mm, "mid": v(-12.53, -8.27) * mm, "end": v(-12.7, -8.2) * mm});
            skLineSegment(sketch, "E265.0.40", {"start": v(-12.7, -8.2) * mm, "end": v(-14.4, -8.2) * mm});
            skArc(sketch, "E265.0.41", {"start": v(-14.4, -8.2) * mm, "mid": v(-15.42, -7.52) * mm, "end": v(-15.18, -6.32) * mm});
            skLineSegment(sketch, "E265.0.42", {"start": v(-15.18, -6.32) * mm, "end": v(-12.9, -4.04) * mm});
            skArc(sketch, "E265.0.43", {"start": v(-12.9, -4.04) * mm, "mid": v(-12.4, -3.72) * mm, "end": v(-11.83, -3.6) * mm});
            skLineSegment(sketch, "E265.0.44", {"start": v(-11.83, -3.6) * mm, "end": v(-8.08, -3.6) * mm});
            skArc(sketch, "E265.0.45", {"start": v(-8.08, -3.6) * mm, "mid": v(-7.5, -3.72) * mm, "end": v(-7.02, -4.04) * mm});
            skLineSegment(sketch, "E265.0.46", {"start": v(-7.02, -4.04) * mm, "end": v(-4.73, -6.32) * mm});
            skArc(sketch, "E265.0.47", {"start": v(-4.73, -6.32) * mm, "mid": v(-4.5, -7.52) * mm, "end": v(-5.51, -8.2) * mm});
            skLineSegment(sketch, "E265.0.48", {"start": v(-5.51, -8.2) * mm, "end": v(-7.2, -8.2) * mm});
            skArc(sketch, "E265.0.49", {"start": v(-7.2, -8.2) * mm, "mid": v(-7.38, -8.27) * mm, "end": v(-7.45, -8.45) * mm});
            skLineSegment(sketch, "E265.0.50", {"start": v(-7.45, -8.45) * mm, "end": v(-7.45, -9.5) * mm});
            skArc(sketch, "E265.0.51", {"start": v(-7.45, -9.5) * mm, "mid": v(-7.3, -9.85) * mm, "end": v(-6.95, -10) * mm});
            skArc(sketch, "E265.0.61", {"start": v(-5.92, -2.94) * mm, "mid": v(-6.24, -2.45) * mm, "end": v(-6.35, -1.88) * mm});
            skLineSegment(sketch, "E265.0.62", {"start": v(-6.35, -1.88) * mm, "end": v(-6.35, 1.88) * mm});
            skArc(sketch, "E265.0.63", {"start": v(-6.35, 1.88) * mm, "mid": v(-6.24, 2.45) * mm, "end": v(-5.92, 2.94) * mm});
            skArc(sketch, "E265.0.73", {"start": v(-6.95, 10) * mm, "mid": v(-7.3, 9.85) * mm, "end": v(-7.45, 9.5) * mm});
            skLineSegment(sketch, "E265.0.74", {"start": v(-7.45, 9.5) * mm, "end": v(-7.45, 8.45) * mm});
            skArc(sketch, "E265.0.75", {"start": v(-7.45, 8.45) * mm, "mid": v(-7.38, 8.27) * mm, "end": v(-7.2, 8.2) * mm});
            skLineSegment(sketch, "E265.0.76", {"start": v(-7.2, 8.2) * mm, "end": v(-5.51, 8.2) * mm});
            skArc(sketch, "E265.0.77", {"start": v(-5.51, 8.2) * mm, "mid": v(-4.5, 7.52) * mm, "end": v(-4.73, 6.32) * mm});
            skLineSegment(sketch, "E265.0.78", {"start": v(-4.73, 6.32) * mm, "end": v(-7.02, 4.04) * mm});
            skArc(sketch, "E265.0.79", {"start": v(-7.02, 4.04) * mm, "mid": v(-7.5, 3.71) * mm, "end": v(-8.08, 3.6) * mm});
            skLineSegment(sketch, "E265.0.80", {"start": v(-8.08, 3.6) * mm, "end": v(-11.83, 3.6) * mm});
            skArc(sketch, "E265.0.81", {"start": v(-11.83, 3.6) * mm, "mid": v(-12.4, 3.71) * mm, "end": v(-12.9, 4.04) * mm});
            skLineSegment(sketch, "E265.0.82", {"start": v(-12.9, 4.04) * mm, "end": v(-15.18, 6.32) * mm});
            skArc(sketch, "E265.0.83", {"start": v(-15.18, 6.32) * mm, "mid": v(-15.42, 7.52) * mm, "end": v(-14.4, 8.2) * mm});
            skLineSegment(sketch, "E265.0.84", {"start": v(-14.4, 8.2) * mm, "end": v(-12.7, 8.2) * mm});
            skArc(sketch, "E265.0.85", {"start": v(-12.7, 8.2) * mm, "mid": v(-12.53, 8.27) * mm, "end": v(-12.45, 8.45) * mm});
            skLineSegment(sketch, "E265.0.86", {"start": v(-12.45, 8.45) * mm, "end": v(-12.45, 9.5) * mm});
            skArc(sketch, "E265.0.87", {"start": v(-12.45, 9.5) * mm, "mid": v(-12.6, 9.85) * mm, "end": v(-12.95, 10) * mm});
            skLineSegment(sketch, "E265.0.88", {"start": v(-12.95, 10) * mm, "end": v(-26.95, 10) * mm});
            skArc(sketch, "E265.0.89", {"start": v(-26.95, 10) * mm, "mid": v(-27.3, 9.85) * mm, "end": v(-27.45, 9.5) * mm});
            skLineSegment(sketch, "E265.0.90", {"start": v(-27.45, 9.5) * mm, "end": v(-27.45, 8.45) * mm});
            skArc(sketch, "E265.0.91", {"start": v(-27.45, 8.45) * mm, "mid": v(-27.38, 8.27) * mm, "end": v(-27.2, 8.2) * mm});
            skLineSegment(sketch, "E265.0.92", {"start": v(-27.2, 8.2) * mm, "end": v(-25.51, 8.2) * mm});
            skArc(sketch, "E265.0.93", {"start": v(-25.51, 8.2) * mm, "mid": v(-24.5, 7.52) * mm, "end": v(-24.73, 6.32) * mm});
            skLineSegment(sketch, "E265.0.94", {"start": v(-24.73, 6.32) * mm, "end": v(-27.02, 4.04) * mm});
            skArc(sketch, "E265.0.95", {"start": v(-27.02, 4.04) * mm, "mid": v(-27.5, 3.71) * mm, "end": v(-28.08, 3.6) * mm});
            skLineSegment(sketch, "E265.0.96", {"start": v(-28.08, 3.6) * mm, "end": v(-31.83, 3.6) * mm});
            skArc(sketch, "E265.0.97", {"start": v(-31.83, 3.6) * mm, "mid": v(-32.4, 3.71) * mm, "end": v(-32.9, 4.04) * mm});
            skLineSegment(sketch, "E265.0.98", {"start": v(-32.9, 4.04) * mm, "end": v(-35.18, 6.32) * mm});
            skArc(sketch, "E265.0.99", {"start": v(-35.18, 6.32) * mm, "mid": v(-35.42, 7.52) * mm, "end": v(-34.4, 8.2) * mm});
            skLineSegment(sketch, "E265.0.100", {"start": v(-34.4, 8.2) * mm, "end": v(-32.7, 8.2) * mm});
            skArc(sketch, "E265.0.101", {"start": v(-32.7, 8.2) * mm, "mid": v(-32.53, 8.27) * mm, "end": v(-32.45, 8.45) * mm});
            skLineSegment(sketch, "E265.0.102", {"start": v(-32.45, 8.45) * mm, "end": v(-32.45, 9.5) * mm});
            skArc(sketch, "E265.0.103", {"start": v(-32.45, 9.5) * mm, "mid": v(-32.6, 9.85) * mm, "end": v(-32.95, 10) * mm});
            skCircle(sketch, "E266.0.0", {"center": v(-29.95, 0) * mm, "radius": 2.15 * mm});
            skCircle(sketch, "E267.0.0", {"center": v(-9.95, 0) * mm, "radius": 2.15 * mm});
            skLineSegment(sketch, "E268.0.0", {"start": v(-21.1, 7.76) * mm, "end": v(-25.92, 2.94) * mm});
            skArc(sketch, "E268.0.1", {"start": v(-25.92, 2.94) * mm, "mid": v(-26.24, 2.45) * mm, "end": v(-26.35, 1.88) * mm});
            skLineSegment(sketch, "E268.0.2", {"start": v(-26.35, 1.88) * mm, "end": v(-26.35, -1.88) * mm});
            skArc(sketch, "E268.0.3", {"start": v(-26.35, -1.88) * mm, "mid": v(-26.24, -2.45) * mm, "end": v(-25.92, -2.94) * mm});
            skLineSegment(sketch, "E268.0.4", {"start": v(-25.92, -2.94) * mm, "end": v(-21.1, -7.76) * mm});
            skArc(sketch, "E268.0.5", {"start": v(-21.1, -7.76) * mm, "mid": v(-20.6, -8.09) * mm, "end": v(-20.03, -8.2) * mm});
            skLineSegment(sketch, "E268.0.6", {"start": v(-20.03, -8.2) * mm, "end": v(-19.88, -8.2) * mm});
            skArc(sketch, "E268.0.7", {"start": v(-19.88, -8.2) * mm, "mid": v(-19.3, -8.09) * mm, "end": v(-18.82, -7.76) * mm});
            skLineSegment(sketch, "E268.0.8", {"start": v(-18.82, -7.76) * mm, "end": v(-14, -2.94) * mm});
            skArc(sketch, "E268.0.9", {"start": v(-14, -2.94) * mm, "mid": v(-13.67, -2.45) * mm, "end": v(-13.55, -1.88) * mm});
            skLineSegment(sketch, "E268.0.10", {"start": v(-13.55, -1.88) * mm, "end": v(-13.55, 1.88) * mm});
            skArc(sketch, "E268.0.11", {"start": v(-13.55, 1.88) * mm, "mid": v(-13.67, 2.45) * mm, "end": v(-14, 2.94) * mm});
            skLineSegment(sketch, "E268.0.12", {"start": v(-14, 2.94) * mm, "end": v(-18.82, 7.76) * mm});
            skArc(sketch, "E268.0.13", {"start": v(-18.82, 7.76) * mm, "mid": v(-19.3, 8.08) * mm, "end": v(-19.88, 8.2) * mm});
            skLineSegment(sketch, "E268.0.14", {"start": v(-19.88, 8.2) * mm, "end": v(-20.03, 8.2) * mm});
            skArc(sketch, "E268.0.15", {"start": v(-20.03, 8.2) * mm, "mid": v(-20.6, 8.08) * mm, "end": v(-21.1, 7.76) * mm});
            skLineSegment(sketch, "E269", {"start": v(0.05, 12.68) * mm, "end": v(0.05, -12.08) * mm, "construction": true});
            skCircle(sketch, "E270.0.MirrorC", {"center": v(10.05, 0) * mm, "radius": 2.15 * mm});
            skCircle(sketch, "E271.0.MirrorC", {"center": v(30.05, 0) * mm, "radius": 2.15 * mm});
            skArc(sketch, "E272.0.MirrorCS", {"start": v(6.45, 1.88) * mm, "mid": v(6.33, 2.45) * mm, "end": v(6, 2.94) * mm});
            skLineSegment(sketch, "E273.0.MirrorCS", {"start": v(6.45, -1.88) * mm, "end": v(6.45, 1.88) * mm});
            skArc(sketch, "E274.0.MirrorCS", {"start": v(6, -2.94) * mm, "mid": v(6.33, -2.45) * mm, "end": v(6.45, -1.88) * mm});
            skArc(sketch, "E275.0.MirrorCS", {"start": v(7.05, 10) * mm, "mid": v(7.4, 9.85) * mm, "end": v(7.55, 9.5) * mm});
            skLineSegment(sketch, "E276.0.MirrorCS", {"start": v(7.55, 9.5) * mm, "end": v(7.55, 8.45) * mm});
            skArc(sketch, "E277.0.MirrorCS", {"start": v(7.55, 8.45) * mm, "mid": v(7.47, 8.27) * mm, "end": v(7.3, 8.2) * mm});
            skLineSegment(sketch, "E278.0.MirrorCS", {"start": v(7.3, 8.2) * mm, "end": v(5.6, 8.2) * mm});
            skArc(sketch, "E279.0.MirrorCS", {"start": v(5.6, 8.2) * mm, "mid": v(4.58, 7.52) * mm, "end": v(4.82, 6.32) * mm});
            skLineSegment(sketch, "E280.0.MirrorCS", {"start": v(4.82, 6.32) * mm, "end": v(7.1, 4.04) * mm});
            skArc(sketch, "E281.0.MirrorCS", {"start": v(7.1, 4.04) * mm, "mid": v(7.6, 3.71) * mm, "end": v(8.17, 3.6) * mm});
            skLineSegment(sketch, "E282.0.MirrorCS", {"start": v(8.17, 3.6) * mm, "end": v(11.92, 3.6) * mm});
            skArc(sketch, "E283.0.MirrorCS", {"start": v(11.92, 3.6) * mm, "mid": v(12.5, 3.71) * mm, "end": v(12.98, 4.04) * mm});
            skLineSegment(sketch, "E284.0.MirrorCS", {"start": v(12.98, 4.04) * mm, "end": v(15.27, 6.32) * mm});
            skArc(sketch, "E285.0.MirrorCS", {"start": v(15.27, 6.32) * mm, "mid": v(15.5, 7.52) * mm, "end": v(14.49, 8.2) * mm});
            skLineSegment(sketch, "E286.0.MirrorCS", {"start": v(14.49, 8.2) * mm, "end": v(12.8, 8.2) * mm});
            skArc(sketch, "E287.0.MirrorCS", {"start": v(12.8, 8.2) * mm, "mid": v(12.62, 8.27) * mm, "end": v(12.55, 8.45) * mm});
            skLineSegment(sketch, "E288.0.MirrorCS", {"start": v(12.55, 8.45) * mm, "end": v(12.55, 9.5) * mm});
            skArc(sketch, "E289.0.MirrorCS", {"start": v(12.55, 9.5) * mm, "mid": v(12.7, 9.85) * mm, "end": v(13.05, 10) * mm});
            skLineSegment(sketch, "E290.0.MirrorCS", {"start": v(13.05, 10) * mm, "end": v(27.05, 10) * mm});
            skArc(sketch, "E291.0.MirrorCS", {"start": v(27.05, 10) * mm, "mid": v(27.4, 9.85) * mm, "end": v(27.55, 9.5) * mm});
            skLineSegment(sketch, "E292.0.MirrorCS", {"start": v(27.55, 9.5) * mm, "end": v(27.55, 8.45) * mm});
            skArc(sketch, "E293.0.MirrorCS", {"start": v(27.55, 8.45) * mm, "mid": v(27.47, 8.27) * mm, "end": v(27.3, 8.2) * mm});
            skLineSegment(sketch, "E294.0.MirrorCS", {"start": v(27.3, 8.2) * mm, "end": v(25.6, 8.2) * mm});
            skArc(sketch, "E295.0.MirrorCS", {"start": v(25.6, 8.2) * mm, "mid": v(24.58, 7.52) * mm, "end": v(24.82, 6.32) * mm});
            skLineSegment(sketch, "E296.0.MirrorCS", {"start": v(24.82, 6.32) * mm, "end": v(27.1, 4.04) * mm});
            skArc(sketch, "E297.0.MirrorCS", {"start": v(27.1, 4.04) * mm, "mid": v(27.6, 3.71) * mm, "end": v(28.17, 3.6) * mm});
            skLineSegment(sketch, "E298.0.MirrorCS", {"start": v(28.17, 3.6) * mm, "end": v(31.92, 3.6) * mm});
            skArc(sketch, "E299.0.MirrorCS", {"start": v(31.92, 3.6) * mm, "mid": v(32.5, 3.71) * mm, "end": v(32.98, 4.04) * mm});
            skLineSegment(sketch, "E300.0.MirrorCS", {"start": v(32.98, 4.04) * mm, "end": v(35.27, 6.32) * mm});
            skArc(sketch, "E301.0.MirrorCS", {"start": v(35.27, 6.32) * mm, "mid": v(35.5, 7.52) * mm, "end": v(34.49, 8.2) * mm});
            skLineSegment(sketch, "E302.0.MirrorCS", {"start": v(34.49, 8.2) * mm, "end": v(32.8, 8.2) * mm});
            skArc(sketch, "E303.0.MirrorCS", {"start": v(32.8, 8.2) * mm, "mid": v(32.62, 8.27) * mm, "end": v(32.55, 8.45) * mm});
            skLineSegment(sketch, "E304.0.MirrorCS", {"start": v(32.55, 8.45) * mm, "end": v(32.55, 9.5) * mm});
            skArc(sketch, "E305.0.MirrorCS", {"start": v(32.55, 9.5) * mm, "mid": v(32.7, 9.85) * mm, "end": v(33.05, 10) * mm});
            skLineSegment(sketch, "E306.0.MirrorCS", {"start": v(33.05, 10) * mm, "end": v(38.55, 10) * mm});
            skArc(sketch, "E307.0.MirrorCS", {"start": v(38.55, 10) * mm, "mid": v(39.6, 9.56) * mm, "end": v(40.05, 8.5) * mm});
            skLineSegment(sketch, "E308.0.MirrorCS", {"start": v(40.05, 8.5) * mm, "end": v(40.05, 3) * mm});
            skArc(sketch, "E309.0.MirrorCS", {"start": v(40.05, 3) * mm, "mid": v(39.9, 2.65) * mm, "end": v(39.55, 2.5) * mm});
            skLineSegment(sketch, "E310.0.MirrorCS", {"start": v(39.55, 2.5) * mm, "end": v(38.5, 2.5) * mm});
            skArc(sketch, "E311.0.MirrorCS", {"start": v(38.5, 2.5) * mm, "mid": v(38.32, 2.57) * mm, "end": v(38.25, 2.75) * mm});
            skLineSegment(sketch, "E312.0.MirrorCS", {"start": v(38.25, 2.75) * mm, "end": v(38.25, 4.44) * mm});
            skArc(sketch, "E313.0.MirrorCS", {"start": v(38.25, 4.44) * mm, "mid": v(37.57, 5.46) * mm, "end": v(36.37, 5.22) * mm});
            skLineSegment(sketch, "E314.0.MirrorCS", {"start": v(36.37, 5.22) * mm, "end": v(34.08, 2.94) * mm});
            skArc(sketch, "E315.0.MirrorCS", {"start": v(34.08, 2.94) * mm, "mid": v(33.76, 2.45) * mm, "end": v(33.65, 1.88) * mm});
            skLineSegment(sketch, "E316.0.MirrorCS", {"start": v(33.65, 1.88) * mm, "end": v(33.65, -1.88) * mm});
            skArc(sketch, "E317.0.MirrorCS", {"start": v(33.65, -1.88) * mm, "mid": v(33.76, -2.45) * mm, "end": v(34.08, -2.94) * mm});
            skLineSegment(sketch, "E318.0.MirrorCS", {"start": v(34.08, -2.94) * mm, "end": v(36.37, -5.22) * mm});
            skArc(sketch, "E319.0.MirrorCS", {"start": v(36.37, -5.22) * mm, "mid": v(37.57, -5.46) * mm, "end": v(38.25, -4.45) * mm});
            skLineSegment(sketch, "E320.0.MirrorCS", {"start": v(38.25, -4.45) * mm, "end": v(38.25, -2.75) * mm});
            skArc(sketch, "E321.0.MirrorCS", {"start": v(38.25, -2.75) * mm, "mid": v(38.32, -2.57) * mm, "end": v(38.5, -2.5) * mm});
            skLineSegment(sketch, "E322.0.MirrorCS", {"start": v(38.5, -2.5) * mm, "end": v(39.55, -2.5) * mm});
            skArc(sketch, "E323.0.MirrorCS", {"start": v(39.55, -2.5) * mm, "mid": v(39.9, -2.65) * mm, "end": v(40.05, -3) * mm});
            skLineSegment(sketch, "E324.0.MirrorCS", {"start": v(40.05, -3) * mm, "end": v(40.05, -8.5) * mm});
            skArc(sketch, "E325.0.MirrorCS", {"start": v(40.05, -8.5) * mm, "mid": v(39.6, -9.56) * mm, "end": v(38.55, -10) * mm});
            skLineSegment(sketch, "E326.0.MirrorCS", {"start": v(38.55, -10) * mm, "end": v(33.05, -10) * mm});
            skArc(sketch, "E327.0.MirrorCS", {"start": v(33.05, -10) * mm, "mid": v(32.7, -9.85) * mm, "end": v(32.55, -9.5) * mm});
            skLineSegment(sketch, "E328.0.MirrorCS", {"start": v(32.55, -9.5) * mm, "end": v(32.55, -8.45) * mm});
            skArc(sketch, "E329.0.MirrorCS", {"start": v(32.55, -8.45) * mm, "mid": v(32.62, -8.27) * mm, "end": v(32.8, -8.2) * mm});
            skLineSegment(sketch, "E330.0.MirrorCS", {"start": v(32.8, -8.2) * mm, "end": v(34.49, -8.2) * mm});
            skArc(sketch, "E331.0.MirrorCS", {"start": v(34.49, -8.2) * mm, "mid": v(35.5, -7.52) * mm, "end": v(35.27, -6.32) * mm});
            skLineSegment(sketch, "E332.0.MirrorCS", {"start": v(35.27, -6.32) * mm, "end": v(32.98, -4.04) * mm});
            skArc(sketch, "E333.0.MirrorCS", {"start": v(32.98, -4.04) * mm, "mid": v(32.5, -3.72) * mm, "end": v(31.92, -3.6) * mm});
            skLineSegment(sketch, "E334.0.MirrorCS", {"start": v(31.92, -3.6) * mm, "end": v(28.17, -3.6) * mm});
            skArc(sketch, "E335.0.MirrorCS", {"start": v(28.17, -3.6) * mm, "mid": v(27.6, -3.72) * mm, "end": v(27.1, -4.04) * mm});
            skLineSegment(sketch, "E336.0.MirrorCS", {"start": v(27.1, -4.04) * mm, "end": v(24.82, -6.32) * mm});
            skArc(sketch, "E337.0.MirrorCS", {"start": v(24.82, -6.32) * mm, "mid": v(24.58, -7.52) * mm, "end": v(25.6, -8.2) * mm});
            skLineSegment(sketch, "E338.0.MirrorCS", {"start": v(25.6, -8.2) * mm, "end": v(27.3, -8.2) * mm});
            skArc(sketch, "E339.0.MirrorCS", {"start": v(27.3, -8.2) * mm, "mid": v(27.47, -8.27) * mm, "end": v(27.55, -8.45) * mm});
            skLineSegment(sketch, "E340.0.MirrorCS", {"start": v(27.55, -8.45) * mm, "end": v(27.55, -9.5) * mm});
            skArc(sketch, "E341.0.MirrorCS", {"start": v(27.55, -9.5) * mm, "mid": v(27.4, -9.85) * mm, "end": v(27.05, -10) * mm});
            skLineSegment(sketch, "E342.0.MirrorCS", {"start": v(27.05, -10) * mm, "end": v(13.05, -10) * mm});
            skArc(sketch, "E343.0.MirrorCS", {"start": v(13.05, -10) * mm, "mid": v(12.7, -9.85) * mm, "end": v(12.55, -9.5) * mm});
            skLineSegment(sketch, "E344.0.MirrorCS", {"start": v(12.55, -9.5) * mm, "end": v(12.55, -8.45) * mm});
            skArc(sketch, "E345.0.MirrorCS", {"start": v(12.55, -8.45) * mm, "mid": v(12.62, -8.27) * mm, "end": v(12.8, -8.2) * mm});
            skLineSegment(sketch, "E346.0.MirrorCS", {"start": v(12.8, -8.2) * mm, "end": v(14.49, -8.2) * mm});
            skArc(sketch, "E347.0.MirrorCS", {"start": v(14.49, -8.2) * mm, "mid": v(15.5, -7.52) * mm, "end": v(15.27, -6.32) * mm});
            skLineSegment(sketch, "E348.0.MirrorCS", {"start": v(15.27, -6.32) * mm, "end": v(12.98, -4.04) * mm});
            skArc(sketch, "E349.0.MirrorCS", {"start": v(12.98, -4.04) * mm, "mid": v(12.5, -3.72) * mm, "end": v(11.92, -3.6) * mm});
            skLineSegment(sketch, "E350.0.MirrorCS", {"start": v(11.92, -3.6) * mm, "end": v(8.17, -3.6) * mm});
            skArc(sketch, "E351.0.MirrorCS", {"start": v(8.17, -3.6) * mm, "mid": v(7.6, -3.72) * mm, "end": v(7.1, -4.04) * mm});
            skLineSegment(sketch, "E352.0.MirrorCS", {"start": v(7.1, -4.04) * mm, "end": v(4.82, -6.32) * mm});
            skArc(sketch, "E353.0.MirrorCS", {"start": v(4.82, -6.32) * mm, "mid": v(4.58, -7.52) * mm, "end": v(5.6, -8.2) * mm});
            skLineSegment(sketch, "E354.0.MirrorCS", {"start": v(5.6, -8.2) * mm, "end": v(7.3, -8.2) * mm});
            skArc(sketch, "E355.0.MirrorCS", {"start": v(7.3, -8.2) * mm, "mid": v(7.47, -8.27) * mm, "end": v(7.55, -8.45) * mm});
            skLineSegment(sketch, "E356.0.MirrorCS", {"start": v(7.55, -8.45) * mm, "end": v(7.55, -9.5) * mm});
            skArc(sketch, "E357.0.MirrorCS", {"start": v(7.55, -9.5) * mm, "mid": v(7.4, -9.85) * mm, "end": v(7.05, -10) * mm});
            skLineSegment(sketch, "E358.0.MirrorCS", {"start": v(13.65, -1.88) * mm, "end": v(13.65, 1.88) * mm});
            skArc(sketch, "E359.0.MirrorCS", {"start": v(13.65, 1.88) * mm, "mid": v(13.76, 2.45) * mm, "end": v(14.08, 2.94) * mm});
            skLineSegment(sketch, "E360.0.MirrorCS", {"start": v(14.08, 2.94) * mm, "end": v(18.9, 7.76) * mm});
            skArc(sketch, "E361.0.MirrorCS", {"start": v(18.9, 7.76) * mm, "mid": v(19.4, 8.08) * mm, "end": v(19.97, 8.2) * mm});
            skLineSegment(sketch, "E362.0.MirrorCS", {"start": v(19.97, 8.2) * mm, "end": v(20.12, 8.2) * mm});
            skArc(sketch, "E363.0.MirrorCS", {"start": v(20.12, 8.2) * mm, "mid": v(20.7, 8.08) * mm, "end": v(21.18, 7.76) * mm});
            skLineSegment(sketch, "E364.0.MirrorCS", {"start": v(21.18, 7.76) * mm, "end": v(26, 2.94) * mm});
            skArc(sketch, "E365.0.MirrorCS", {"start": v(26, 2.94) * mm, "mid": v(26.33, 2.45) * mm, "end": v(26.45, 1.88) * mm});
            skLineSegment(sketch, "E366.0.MirrorCS", {"start": v(26.45, 1.88) * mm, "end": v(26.45, -1.88) * mm});
            skArc(sketch, "E367.0.MirrorCS", {"start": v(26.45, -1.88) * mm, "mid": v(26.33, -2.45) * mm, "end": v(26, -2.94) * mm});
            skLineSegment(sketch, "E368.0.MirrorCS", {"start": v(26, -2.94) * mm, "end": v(21.18, -7.76) * mm});
            skArc(sketch, "E369.0.MirrorCS", {"start": v(21.18, -7.76) * mm, "mid": v(20.7, -8.09) * mm, "end": v(20.12, -8.2) * mm});
            skLineSegment(sketch, "E370.0.MirrorCS", {"start": v(20.12, -8.2) * mm, "end": v(19.97, -8.2) * mm});
            skArc(sketch, "E371.0.MirrorCS", {"start": v(19.97, -8.2) * mm, "mid": v(19.4, -8.09) * mm, "end": v(18.9, -7.76) * mm});
            skLineSegment(sketch, "E372.0.MirrorCS", {"start": v(18.9, -7.76) * mm, "end": v(14.08, -2.94) * mm});
            skArc(sketch, "E373.0.MirrorCS", {"start": v(14.08, -2.94) * mm, "mid": v(13.76, -2.45) * mm, "end": v(13.65, -1.88) * mm});
            skLineSegment(sketch, "E374", {"start": v(-6.95, 10) * mm, "end": v(7.05, 10) * mm});
            skLineSegment(sketch, "E375", {"start": v(-6.95, -10) * mm, "end": v(7.05, -10) * mm});
            skLineSegment(sketch, "E376", {"start": v(-9.95, 12.57) * mm, "end": v(-9.95, -12.55) * mm, "construction": true});
            skLineSegment(sketch, "E377.0.MirrorCS", {"start": v(-1.1, -7.76) * mm, "end": v(-5.92, -2.94) * mm});
            skLineSegment(sketch, "E378.0.MirrorCS", {"start": v(-5.92, 2.94) * mm, "end": v(-1.1, 7.76) * mm});
            skLineSegment(sketch, "E379.0.MirrorCS", {"start": v(1.18, 7.76) * mm, "end": v(6, 2.94) * mm});
            skLineSegment(sketch, "E380.0.MirrorCS", {"start": v(6, -2.94) * mm, "end": v(1.18, -7.76) * mm});
            skArc(sketch, "E381.0.MirrorCS", {"start": v(0.12, 8.2) * mm, "mid": v(0.7, 8.08) * mm, "end": v(1.18, 7.76) * mm});
            skArc(sketch, "E382.0.MirrorCS", {"start": v(-1.1, 7.76) * mm, "mid": v(-0.6, 8.08) * mm, "end": v(-0.03, 8.2) * mm});
            skArc(sketch, "E383.0.MirrorCS", {"start": v(1.18, -7.76) * mm, "mid": v(0.7, -8.09) * mm, "end": v(0.12, -8.2) * mm});
            skArc(sketch, "E384.0.MirrorCS", {"start": v(-0.03, -8.2) * mm, "mid": v(-0.6, -8.09) * mm, "end": v(-1.1, -7.76) * mm});
            skLineSegment(sketch, "E385.0.MirrorCS", {"start": v(0.12, -8.2) * mm, "end": v(-0.03, -8.2) * mm});
            skLineSegment(sketch, "E386.0.MirrorCS", {"start": v(-0.03, 8.2) * mm, "end": v(0.12, 8.2) * mm});
            skSolve(sketch);
        }
        {
            var Q0;
            Q0=qCreatedBy(makeId("Front.planeOp"),FACE);
            var sketch = newSketch(context, id + "F4", { "sketchPlane" : qUnion([Q0])});
            skLineSegment(sketch, "E387.0.0", {"start": v(-13.03, 15.78) * mm, "end": v(-18.53, 15.78) * mm});
            skArc(sketch, "E387.0.1", {"start": v(-18.53, 15.78) * mm, "mid": v(-19.6, 15.34) * mm, "end": v(-20.03, 14.28) * mm});
            skLineSegment(sketch, "E387.0.2", {"start": v(-20.03, 14.28) * mm, "end": v(-20.03, 8.78) * mm});
            skArc(sketch, "E387.0.3", {"start": v(-20.03, 8.78) * mm, "mid": v(-19.89, 8.42) * mm, "end": v(-19.53, 8.28) * mm});
            skLineSegment(sketch, "E387.0.4", {"start": v(-19.53, 8.28) * mm, "end": v(-18.48, 8.28) * mm});
            skArc(sketch, "E387.0.5", {"start": v(-18.48, 8.28) * mm, "mid": v(-18.3, 8.35) * mm, "end": v(-18.23, 8.53) * mm});
            skLineSegment(sketch, "E387.0.6", {"start": v(-18.23, 8.53) * mm, "end": v(-18.23, 10.22) * mm});
            skArc(sketch, "E387.0.7", {"start": v(-18.23, 10.22) * mm, "mid": v(-17.55, 11.24) * mm, "end": v(-16.35, 11) * mm});
            skLineSegment(sketch, "E387.0.8", {"start": v(-16.35, 11) * mm, "end": v(-14.07, 8.72) * mm});
            skArc(sketch, "E387.0.9", {"start": v(-14.07, 8.72) * mm, "mid": v(-13.75, 8.23) * mm, "end": v(-13.63, 7.66) * mm});
            skLineSegment(sketch, "E387.0.10", {"start": v(-13.63, 7.66) * mm, "end": v(-13.63, 3.9) * mm});
            skArc(sketch, "E387.0.11", {"start": v(-13.63, 3.9) * mm, "mid": v(-13.75, 3.32) * mm, "end": v(-14.07, 2.84) * mm});
            skLineSegment(sketch, "E387.0.12", {"start": v(-14.07, 2.84) * mm, "end": v(-16.35, 0.55) * mm});
            skArc(sketch, "E387.0.13", {"start": v(-16.35, 0.55) * mm, "mid": v(-17.55, 0.32) * mm, "end": v(-18.23, 1.33) * mm});
            skLineSegment(sketch, "E387.0.14", {"start": v(-18.23, 1.33) * mm, "end": v(-18.23, 3.03) * mm});
            skArc(sketch, "E387.0.15", {"start": v(-18.23, 3.03) * mm, "mid": v(-18.3, 3.2) * mm, "end": v(-18.48, 3.28) * mm});
            skLineSegment(sketch, "E387.0.16", {"start": v(-18.48, 3.28) * mm, "end": v(-19.53, 3.28) * mm});
            skArc(sketch, "E387.0.17", {"start": v(-19.53, 3.28) * mm, "mid": v(-19.89, 3.13) * mm, "end": v(-20.03, 2.78) * mm});
            skArc(sketch, "E387.0.27", {"start": v(-12.97, 1.74) * mm, "mid": v(-12.48, 2.06) * mm, "end": v(-11.91, 2.18) * mm});
            skLineSegment(sketch, "E387.0.28", {"start": v(-11.91, 2.18) * mm, "end": v(-8.15, 2.18) * mm});
            skLineSegment(sketch, "E387.0.44", {"start": v(8.09, 2.18) * mm, "end": v(11.85, 2.18) * mm});
            skArc(sketch, "E387.0.45", {"start": v(11.85, 2.18) * mm, "mid": v(12.42, 2.06) * mm, "end": v(12.9, 1.74) * mm});
            skArc(sketch, "E387.0.55", {"start": v(19.97, 2.78) * mm, "mid": v(19.82, 3.13) * mm, "end": v(19.47, 3.28) * mm});
            skLineSegment(sketch, "E387.0.56", {"start": v(19.47, 3.28) * mm, "end": v(18.42, 3.28) * mm});
            skArc(sketch, "E387.0.57", {"start": v(18.42, 3.28) * mm, "mid": v(18.24, 3.2) * mm, "end": v(18.17, 3.03) * mm});
            skLineSegment(sketch, "E387.0.58", {"start": v(18.17, 3.03) * mm, "end": v(18.17, 1.33) * mm});
            skArc(sketch, "E387.0.59", {"start": v(18.17, 1.33) * mm, "mid": v(17.49, 0.32) * mm, "end": v(16.3, 0.55) * mm});
            skLineSegment(sketch, "E387.0.60", {"start": v(16.3, 0.55) * mm, "end": v(14, 2.84) * mm});
            skArc(sketch, "E387.0.61", {"start": v(14, 2.84) * mm, "mid": v(13.68, 3.32) * mm, "end": v(13.57, 3.9) * mm});
            skLineSegment(sketch, "E387.0.62", {"start": v(13.57, 3.9) * mm, "end": v(13.57, 7.66) * mm});
            skArc(sketch, "E387.0.63", {"start": v(13.57, 7.66) * mm, "mid": v(13.68, 8.23) * mm, "end": v(14, 8.72) * mm});
            skLineSegment(sketch, "E387.0.64", {"start": v(14, 8.72) * mm, "end": v(16.3, 11) * mm});
            skArc(sketch, "E387.0.65", {"start": v(16.3, 11) * mm, "mid": v(17.49, 11.24) * mm, "end": v(18.17, 10.22) * mm});
            skLineSegment(sketch, "E387.0.66", {"start": v(18.17, 10.22) * mm, "end": v(18.17, 8.53) * mm});
            skArc(sketch, "E387.0.67", {"start": v(18.17, 8.53) * mm, "mid": v(18.24, 8.35) * mm, "end": v(18.42, 8.28) * mm});
            skLineSegment(sketch, "E387.0.68", {"start": v(18.42, 8.28) * mm, "end": v(19.47, 8.28) * mm});
            skArc(sketch, "E387.0.69", {"start": v(19.47, 8.28) * mm, "mid": v(19.82, 8.42) * mm, "end": v(19.97, 8.78) * mm});
            skLineSegment(sketch, "E387.0.70", {"start": v(19.97, 8.78) * mm, "end": v(19.97, 14.28) * mm});
            skArc(sketch, "E387.0.71", {"start": v(19.97, 14.28) * mm, "mid": v(19.53, 15.34) * mm, "end": v(18.47, 15.78) * mm});
            skLineSegment(sketch, "E387.0.72", {"start": v(18.47, 15.78) * mm, "end": v(12.97, 15.78) * mm});
            skArc(sketch, "E387.0.73", {"start": v(12.97, 15.78) * mm, "mid": v(12.61, 15.63) * mm, "end": v(12.47, 15.28) * mm});
            skLineSegment(sketch, "E387.0.74", {"start": v(12.47, 15.28) * mm, "end": v(12.47, 14.23) * mm});
            skArc(sketch, "E387.0.75", {"start": v(12.47, 14.23) * mm, "mid": v(12.54, 14.05) * mm, "end": v(12.72, 13.98) * mm});
            skLineSegment(sketch, "E387.0.76", {"start": v(12.72, 13.98) * mm, "end": v(14.41, 13.98) * mm});
            skArc(sketch, "E387.0.77", {"start": v(14.41, 13.98) * mm, "mid": v(15.43, 13.3) * mm, "end": v(15.2, 12.1) * mm});
            skLineSegment(sketch, "E387.0.78", {"start": v(15.2, 12.1) * mm, "end": v(12.9, 9.82) * mm});
            skArc(sketch, "E387.0.79", {"start": v(12.9, 9.82) * mm, "mid": v(12.42, 9.5) * mm, "end": v(11.85, 9.38) * mm});
            skLineSegment(sketch, "E387.0.80", {"start": v(11.85, 9.38) * mm, "end": v(8.09, 9.38) * mm});
            skArc(sketch, "E387.0.81", {"start": v(8.09, 9.38) * mm, "mid": v(7.52, 9.5) * mm, "end": v(7.03, 9.82) * mm});
            skLineSegment(sketch, "E387.0.82", {"start": v(7.03, 9.82) * mm, "end": v(4.75, 12.1) * mm});
            skArc(sketch, "E387.0.83", {"start": v(4.75, 12.1) * mm, "mid": v(4.5, 13.3) * mm, "end": v(5.52, 13.98) * mm});
            skLineSegment(sketch, "E387.0.84", {"start": v(5.52, 13.98) * mm, "end": v(7.22, 13.98) * mm});
            skArc(sketch, "E387.0.85", {"start": v(7.22, 13.98) * mm, "mid": v(7.4, 14.05) * mm, "end": v(7.47, 14.23) * mm});
            skLineSegment(sketch, "E387.0.86", {"start": v(7.47, 14.23) * mm, "end": v(7.47, 15.28) * mm});
            skArc(sketch, "E387.0.87", {"start": v(7.47, 15.28) * mm, "mid": v(7.32, 15.63) * mm, "end": v(6.97, 15.78) * mm});
            skLineSegment(sketch, "E387.0.88", {"start": v(6.97, 15.78) * mm, "end": v(-7.03, 15.78) * mm});
            skArc(sketch, "E387.0.89", {"start": v(-7.03, 15.78) * mm, "mid": v(-7.39, 15.63) * mm, "end": v(-7.53, 15.28) * mm});
            skLineSegment(sketch, "E387.0.90", {"start": v(-7.53, 15.28) * mm, "end": v(-7.53, 14.23) * mm});
            skArc(sketch, "E387.0.91", {"start": v(-7.53, 14.23) * mm, "mid": v(-7.46, 14.05) * mm, "end": v(-7.28, 13.98) * mm});
            skLineSegment(sketch, "E387.0.92", {"start": v(-7.28, 13.98) * mm, "end": v(-5.59, 13.98) * mm});
            skArc(sketch, "E387.0.93", {"start": v(-5.59, 13.98) * mm, "mid": v(-4.57, 13.3) * mm, "end": v(-4.8, 12.1) * mm});
            skLineSegment(sketch, "E387.0.94", {"start": v(-4.8, 12.1) * mm, "end": v(-7.1, 9.82) * mm});
            skArc(sketch, "E387.0.95", {"start": v(-7.1, 9.82) * mm, "mid": v(-7.58, 9.5) * mm, "end": v(-8.15, 9.38) * mm});
            skLineSegment(sketch, "E387.0.96", {"start": v(-8.15, 9.38) * mm, "end": v(-11.91, 9.38) * mm});
            skArc(sketch, "E387.0.97", {"start": v(-11.91, 9.38) * mm, "mid": v(-12.48, 9.5) * mm, "end": v(-12.97, 9.82) * mm});
            skLineSegment(sketch, "E387.0.98", {"start": v(-12.97, 9.82) * mm, "end": v(-15.25, 12.1) * mm});
            skArc(sketch, "E387.0.99", {"start": v(-15.25, 12.1) * mm, "mid": v(-15.5, 13.3) * mm, "end": v(-14.48, 13.98) * mm});
            skLineSegment(sketch, "E387.0.100", {"start": v(-14.48, 13.98) * mm, "end": v(-12.78, 13.98) * mm});
            skArc(sketch, "E387.0.101", {"start": v(-12.78, 13.98) * mm, "mid": v(-12.6, 14.05) * mm, "end": v(-12.53, 14.23) * mm});
            skLineSegment(sketch, "E387.0.102", {"start": v(-12.53, 14.23) * mm, "end": v(-12.53, 15.28) * mm});
            skArc(sketch, "E387.0.103", {"start": v(-12.53, 15.28) * mm, "mid": v(-12.68, 15.63) * mm, "end": v(-13.03, 15.78) * mm});
            skCircle(sketch, "E388.0", {"center": v(-10.03, 5.78) * mm, "radius": 2.15 * mm});
            skLineSegment(sketch, "E389.0.0", {"start": v(-1.17, 13.54) * mm, "end": v(-6, 8.72) * mm});
            skArc(sketch, "E389.0.1", {"start": v(-6, 8.72) * mm, "mid": v(-6.32, 8.23) * mm, "end": v(-6.43, 7.66) * mm});
            skLineSegment(sketch, "E389.0.2", {"start": v(-6.43, 7.66) * mm, "end": v(-6.43, 3.9) * mm});
            skLineSegment(sketch, "E389.0.10", {"start": v(6.37, 3.9) * mm, "end": v(6.37, 7.66) * mm});
            skArc(sketch, "E389.0.11", {"start": v(6.37, 7.66) * mm, "mid": v(6.25, 8.23) * mm, "end": v(5.93, 8.72) * mm});
            skLineSegment(sketch, "E389.0.12", {"start": v(5.93, 8.72) * mm, "end": v(1.1, 13.54) * mm});
            skArc(sketch, "E389.0.13", {"start": v(1.1, 13.54) * mm, "mid": v(0.62, 13.86) * mm, "end": v(0.05, 13.98) * mm});
            skLineSegment(sketch, "E389.0.14", {"start": v(0.05, 13.98) * mm, "end": v(-0.11, 13.98) * mm});
            skArc(sketch, "E389.0.15", {"start": v(-0.11, 13.98) * mm, "mid": v(-0.68, 13.86) * mm, "end": v(-1.17, 13.54) * mm});
            skCircle(sketch, "E390.0.0", {"center": v(9.97, 5.78) * mm, "radius": 2.15 * mm});
            skLineSegment(sketch, "E391.1", {"start": v(-18.53, 15.78) * mm, "end": v(-13.03, 15.78) * mm});
            skLineSegment(sketch, "E391.3", {"start": v(-12.53, 15.28) * mm, "end": v(-12.53, 14.23) * mm});
            skLineSegment(sketch, "E391.5", {"start": v(-12.78, 13.98) * mm, "end": v(-14.48, 13.98) * mm});
            skArc(sketch, "E391.6", {"start": v(-14.48, 13.98) * mm, "mid": v(-15.5, 13.3) * mm, "end": v(-15.25, 12.1) * mm});
            skArc(sketch, "E391.8", {"start": v(-12.97, 9.82) * mm, "mid": v(-12.48, 9.5) * mm, "end": v(-11.91, 9.38) * mm});
            skLineSegment(sketch, "E391.9", {"start": v(-11.91, 9.38) * mm, "end": v(-8.15, 9.38) * mm});
            skArc(sketch, "E391.10", {"start": v(-8.15, 9.38) * mm, "mid": v(-7.58, 9.5) * mm, "end": v(-7.1, 9.82) * mm});
            skLineSegment(sketch, "E391.11", {"start": v(-7.1, 9.82) * mm, "end": v(-4.8, 12.1) * mm});
            skArc(sketch, "E391.12", {"start": v(-4.8, 12.1) * mm, "mid": v(-4.57, 13.3) * mm, "end": v(-5.59, 13.98) * mm});
            skLineSegment(sketch, "E391.13", {"start": v(-5.59, 13.98) * mm, "end": v(-7.28, 13.98) * mm});
            skLineSegment(sketch, "E391.19", {"start": v(-18.48, 8.28) * mm, "end": v(-19.53, 8.28) * mm});
            skLineSegment(sketch, "E391.21", {"start": v(-18.23, 10.22) * mm, "end": v(-18.23, 8.53) * mm});
            skArc(sketch, "E391.22", {"start": v(-16.35, 11) * mm, "mid": v(-17.55, 11.24) * mm, "end": v(-18.23, 10.22) * mm});
            skLineSegment(sketch, "E391.23", {"start": v(-14.07, 8.72) * mm, "end": v(-16.35, 11) * mm});
            skArc(sketch, "E391.24", {"start": v(-13.63, 7.66) * mm, "mid": v(-13.75, 8.23) * mm, "end": v(-14.07, 8.72) * mm});
            skArc(sketch, "E391.26", {"start": v(-14.07, 2.84) * mm, "mid": v(-13.75, 3.32) * mm, "end": v(-13.63, 3.9) * mm});
            skArc(sketch, "E391.28", {"start": v(-18.23, 1.33) * mm, "mid": v(-17.55, 0.32) * mm, "end": v(-16.35, 0.55) * mm});
            skLineSegment(sketch, "E391.29", {"start": v(-18.23, 3.03) * mm, "end": v(-18.23, 1.33) * mm});
            skArc(sketch, "E391.42", {"start": v(-11.91, 2.18) * mm, "mid": v(-12.48, 2.06) * mm, "end": v(-12.97, 1.74) * mm});
            skArc(sketch, "E391.57", {"start": v(5.93, 8.72) * mm, "mid": v(6.25, 8.23) * mm, "end": v(6.37, 7.66) * mm});
            skLineSegment(sketch, "E391.58", {"start": v(6.37, 7.66) * mm, "end": v(6.37, 3.9) * mm});
            skArc(sketch, "E391.64", {"start": v(6.97, 15.78) * mm, "mid": v(7.32, 15.63) * mm, "end": v(7.47, 15.28) * mm});
            skLineSegment(sketch, "E391.65", {"start": v(7.47, 15.28) * mm, "end": v(7.47, 14.23) * mm});
            skArc(sketch, "E391.66", {"start": v(7.47, 14.23) * mm, "mid": v(7.4, 14.05) * mm, "end": v(7.22, 13.98) * mm});
            skLineSegment(sketch, "E391.73", {"start": v(12.9, 9.82) * mm, "end": v(15.2, 12.1) * mm});
            skArc(sketch, "E391.76", {"start": v(12.72, 13.98) * mm, "mid": v(12.54, 14.05) * mm, "end": v(12.47, 14.23) * mm});
            skArc(sketch, "E391.78", {"start": v(12.47, 15.28) * mm, "mid": v(12.61, 15.63) * mm, "end": v(12.97, 15.78) * mm});
            skArc(sketch, "E391.80", {"start": v(18.47, 15.78) * mm, "mid": v(19.53, 15.34) * mm, "end": v(19.97, 14.28) * mm});
            skLineSegment(sketch, "E391.81", {"start": v(19.97, 14.28) * mm, "end": v(19.97, 8.78) * mm});
            skArc(sketch, "E391.82", {"start": v(19.97, 8.78) * mm, "mid": v(19.82, 8.42) * mm, "end": v(19.47, 8.28) * mm});
            skArc(sketch, "E391.84", {"start": v(18.42, 8.28) * mm, "mid": v(18.24, 8.35) * mm, "end": v(18.17, 8.53) * mm});
            skLineSegment(sketch, "E391.89", {"start": v(13.57, 7.66) * mm, "end": v(13.57, 3.9) * mm});
            skLineSegment(sketch, "E391.92", {"start": v(14, 2.84) * mm, "end": v(16.3, 0.55) * mm});
            skArc(sketch, "E391.95", {"start": v(18.17, 3.03) * mm, "mid": v(18.24, 3.2) * mm, "end": v(18.42, 3.28) * mm});
            skLineSegment(sketch, "E391.96", {"start": v(18.42, 3.28) * mm, "end": v(19.47, 3.28) * mm});
            skArc(sketch, "E391.97", {"start": v(19.47, 3.28) * mm, "mid": v(19.82, 3.13) * mm, "end": v(19.97, 2.78) * mm});
            skLineSegment(sketch, "E391.108", {"start": v(11.85, 2.18) * mm, "end": v(8.09, 2.18) * mm});
            skLineSegment(sketch, "E391.116", {"start": v(-7.03, 15.78) * mm, "end": v(6.97, 15.78) * mm});
            skLineSegment(sketch, "E391.117", {"start": v(-6, 8.72) * mm, "end": v(-1.17, 13.54) * mm});
            skLineSegment(sketch, "E391.118", {"start": v(1.1, 13.54) * mm, "end": v(5.93, 8.72) * mm});
            skLineSegment(sketch, "E392", {"start": v(-22.16, -4.22) * mm, "end": v(22.53, -4.22) * mm, "construction": true});
            skLineSegment(sketch, "E393", {"start": v(-18.53, 14.28) * mm, "end": v(3.92, -8.17) * mm, "construction": true});
            skArc(sketch, "E394.0.MirrorCS", {"start": v(-19.53, -11.72) * mm, "mid": v(-19.89, -11.58) * mm, "end": v(-20.03, -11.22) * mm});
            skLineSegment(sketch, "E395.0.MirrorCS", {"start": v(-18.48, -11.72) * mm, "end": v(-19.53, -11.72) * mm});
            skArc(sketch, "E396.0.MirrorCS", {"start": v(-18.23, -11.47) * mm, "mid": v(-18.3, -11.65) * mm, "end": v(-18.48, -11.72) * mm});
            skLineSegment(sketch, "E397.0.MirrorCS", {"start": v(-18.23, -11.47) * mm, "end": v(-18.23, -9.78) * mm});
            skArc(sketch, "E398.0.MirrorCS", {"start": v(-16.35, -9) * mm, "mid": v(-17.55, -8.76) * mm, "end": v(-18.23, -9.78) * mm});
            skLineSegment(sketch, "E399.0.MirrorCS", {"start": v(-14.07, -11.28) * mm, "end": v(-16.35, -9) * mm});
            skArc(sketch, "E400.0.MirrorCS", {"start": v(-13.63, -12.34) * mm, "mid": v(-13.75, -11.77) * mm, "end": v(-14.07, -11.28) * mm});
            skLineSegment(sketch, "E401.0.MirrorCS", {"start": v(-13.63, -16.1) * mm, "end": v(-13.63, -12.34) * mm});
            skArc(sketch, "E402.0.MirrorCS", {"start": v(-14.07, -17.16) * mm, "mid": v(-13.75, -16.68) * mm, "end": v(-13.63, -16.1) * mm});
            skLineSegment(sketch, "E403.0.MirrorCS", {"start": v(-16.35, -19.45) * mm, "end": v(-14.07, -17.16) * mm});
            skArc(sketch, "E404.0.MirrorCS", {"start": v(-18.23, -18.67) * mm, "mid": v(-17.55, -19.68) * mm, "end": v(-16.35, -19.45) * mm});
            skLineSegment(sketch, "E405.0.MirrorCS", {"start": v(-18.23, -16.97) * mm, "end": v(-18.23, -18.67) * mm});
            skArc(sketch, "E406.0.MirrorCS", {"start": v(-18.48, -16.72) * mm, "mid": v(-18.3, -16.8) * mm, "end": v(-18.23, -16.97) * mm});
            skLineSegment(sketch, "E407.0.MirrorCS", {"start": v(-19.53, -16.72) * mm, "end": v(-18.48, -16.72) * mm});
            skArc(sketch, "E408.0.MirrorCS", {"start": v(-20.03, -17.22) * mm, "mid": v(-19.89, -16.87) * mm, "end": v(-19.53, -16.72) * mm});
            skLineSegment(sketch, "E409.0.MirrorCS", {"start": v(-20.03, -22.72) * mm, "end": v(-20.03, -17.22) * mm});
            skArc(sketch, "E410.0.MirrorCS", {"start": v(-18.53, -24.22) * mm, "mid": v(-19.6, -23.78) * mm, "end": v(-20.03, -22.72) * mm});
            skLineSegment(sketch, "E411.0.MirrorCS", {"start": v(-18.53, -24.22) * mm, "end": v(-13.03, -24.22) * mm});
            skArc(sketch, "E412.0.MirrorCS", {"start": v(-12.53, -23.72) * mm, "mid": v(-12.68, -24.08) * mm, "end": v(-13.03, -24.22) * mm});
            skLineSegment(sketch, "E413.0.MirrorCS", {"start": v(-12.53, -23.72) * mm, "end": v(-12.53, -22.67) * mm});
            skArc(sketch, "E414.0.MirrorCS", {"start": v(-12.78, -22.42) * mm, "mid": v(-12.6, -22.5) * mm, "end": v(-12.53, -22.67) * mm});
            skLineSegment(sketch, "E415.0.MirrorCS", {"start": v(-12.78, -22.42) * mm, "end": v(-14.48, -22.42) * mm});
            skArc(sketch, "E416.0.MirrorCS", {"start": v(-14.48, -22.42) * mm, "mid": v(-15.5, -21.74) * mm, "end": v(-15.25, -20.55) * mm});
            skLineSegment(sketch, "E417.0.MirrorCS", {"start": v(-12.97, -18.26) * mm, "end": v(-15.25, -20.55) * mm});
            skArc(sketch, "E418.0.MirrorCS", {"start": v(-12.97, -18.26) * mm, "mid": v(-12.48, -17.94) * mm, "end": v(-11.91, -17.82) * mm});
            skLineSegment(sketch, "E419.0.MirrorCS", {"start": v(-8.15, -17.82) * mm, "end": v(-11.91, -17.82) * mm});
            skArc(sketch, "E420.0.MirrorCS", {"start": v(-7.1, -18.26) * mm, "mid": v(-7.58, -17.94) * mm, "end": v(-8.15, -17.82) * mm});
            skLineSegment(sketch, "E421.0.MirrorCS", {"start": v(-4.8, -20.55) * mm, "end": v(-7.1, -18.26) * mm});
            skArc(sketch, "E422.0.MirrorCS", {"start": v(-5.59, -22.42) * mm, "mid": v(-4.57, -21.74) * mm, "end": v(-4.8, -20.55) * mm});
            skLineSegment(sketch, "E423.0.MirrorCS", {"start": v(-5.59, -22.42) * mm, "end": v(-7.28, -22.42) * mm});
            skArc(sketch, "E424.0.MirrorCS", {"start": v(-7.53, -22.67) * mm, "mid": v(-7.46, -22.5) * mm, "end": v(-7.28, -22.42) * mm});
            skLineSegment(sketch, "E425.0.MirrorCS", {"start": v(-7.53, -23.72) * mm, "end": v(-7.53, -22.67) * mm});
            skArc(sketch, "E426.0.MirrorCS", {"start": v(-7.03, -24.22) * mm, "mid": v(-7.39, -24.08) * mm, "end": v(-7.53, -23.72) * mm});
            skLineSegment(sketch, "E427.0.MirrorCS", {"start": v(-7.03, -24.22) * mm, "end": v(6.97, -24.22) * mm});
            skArc(sketch, "E428.0.MirrorCS", {"start": v(6.97, -24.22) * mm, "mid": v(7.32, -24.08) * mm, "end": v(7.47, -23.72) * mm});
            skLineSegment(sketch, "E429.0.MirrorCS", {"start": v(7.47, -22.67) * mm, "end": v(7.47, -23.72) * mm});
            skArc(sketch, "E430.0.MirrorCS", {"start": v(7.22, -22.42) * mm, "mid": v(7.4, -22.5) * mm, "end": v(7.47, -22.67) * mm});
            skLineSegment(sketch, "E431.0.MirrorCS", {"start": v(5.52, -22.42) * mm, "end": v(7.22, -22.42) * mm});
            skArc(sketch, "E432.0.MirrorCS", {"start": v(4.75, -20.55) * mm, "mid": v(4.5, -21.74) * mm, "end": v(5.52, -22.42) * mm});
            skLineSegment(sketch, "E433.0.MirrorCS", {"start": v(7.03, -18.26) * mm, "end": v(4.75, -20.55) * mm});
            skArc(sketch, "E434.0.MirrorCS", {"start": v(8.09, -17.82) * mm, "mid": v(7.52, -17.94) * mm, "end": v(7.03, -18.26) * mm});
            skLineSegment(sketch, "E435.0.MirrorCS", {"start": v(11.85, -17.82) * mm, "end": v(8.09, -17.82) * mm});
            skArc(sketch, "E436.0.MirrorCS", {"start": v(12.9, -18.26) * mm, "mid": v(12.42, -17.94) * mm, "end": v(11.85, -17.82) * mm});
            skLineSegment(sketch, "E437.0.MirrorCS", {"start": v(15.2, -20.55) * mm, "end": v(12.9, -18.26) * mm});
            skArc(sketch, "E438.0.MirrorCS", {"start": v(14.41, -22.42) * mm, "mid": v(15.43, -21.74) * mm, "end": v(15.2, -20.55) * mm});
            skLineSegment(sketch, "E439.0.MirrorCS", {"start": v(12.72, -22.42) * mm, "end": v(14.41, -22.42) * mm});
            skArc(sketch, "E440.0.MirrorCS", {"start": v(12.72, -22.42) * mm, "mid": v(12.54, -22.5) * mm, "end": v(12.47, -22.67) * mm});
            skLineSegment(sketch, "E441.0.MirrorCS", {"start": v(12.47, -23.72) * mm, "end": v(12.47, -22.67) * mm});
            skArc(sketch, "E442.0.MirrorCS", {"start": v(12.97, -24.22) * mm, "mid": v(12.61, -24.08) * mm, "end": v(12.47, -23.72) * mm});
            skLineSegment(sketch, "E443.0.MirrorCS", {"start": v(18.47, -24.22) * mm, "end": v(12.97, -24.22) * mm});
            skArc(sketch, "E444.0.MirrorCS", {"start": v(18.47, -24.22) * mm, "mid": v(19.53, -23.78) * mm, "end": v(19.97, -22.72) * mm});
            skLineSegment(sketch, "E445.0.MirrorCS", {"start": v(19.97, -17.22) * mm, "end": v(19.97, -22.72) * mm});
            skArc(sketch, "E446.0.MirrorCS", {"start": v(19.47, -16.72) * mm, "mid": v(19.82, -16.87) * mm, "end": v(19.97, -17.22) * mm});
            skLineSegment(sketch, "E447.0.MirrorCS", {"start": v(18.42, -16.72) * mm, "end": v(19.47, -16.72) * mm});
            skArc(sketch, "E448.0.MirrorCS", {"start": v(18.42, -16.72) * mm, "mid": v(18.24, -16.8) * mm, "end": v(18.17, -16.97) * mm});
            skLineSegment(sketch, "E449.0.MirrorCS", {"start": v(18.17, -18.67) * mm, "end": v(18.17, -16.97) * mm});
            skArc(sketch, "E450.0.MirrorCS", {"start": v(16.3, -19.45) * mm, "mid": v(17.49, -19.68) * mm, "end": v(18.17, -18.67) * mm});
            skLineSegment(sketch, "E451.0.MirrorCS", {"start": v(14, -17.16) * mm, "end": v(16.3, -19.45) * mm});
            skArc(sketch, "E452.0.MirrorCS", {"start": v(13.57, -16.1) * mm, "mid": v(13.68, -16.68) * mm, "end": v(14, -17.16) * mm});
            skLineSegment(sketch, "E453.0.MirrorCS", {"start": v(13.57, -12.34) * mm, "end": v(13.57, -16.1) * mm});
            skArc(sketch, "E454.0.MirrorCS", {"start": v(14, -11.28) * mm, "mid": v(13.68, -11.77) * mm, "end": v(13.57, -12.34) * mm});
            skLineSegment(sketch, "E455.0.MirrorCS", {"start": v(14, -11.28) * mm, "end": v(16.3, -9) * mm});
            skArc(sketch, "E456.0.MirrorCS", {"start": v(18.17, -9.78) * mm, "mid": v(17.49, -8.76) * mm, "end": v(16.3, -9) * mm});
            skLineSegment(sketch, "E457.0.MirrorCS", {"start": v(18.17, -11.47) * mm, "end": v(18.17, -9.78) * mm});
            skArc(sketch, "E458.0.MirrorCS", {"start": v(18.17, -11.47) * mm, "mid": v(18.24, -11.65) * mm, "end": v(18.42, -11.72) * mm});
            skLineSegment(sketch, "E459.0.MirrorCS", {"start": v(18.42, -11.72) * mm, "end": v(19.47, -11.72) * mm});
            skArc(sketch, "E460.0.MirrorCS", {"start": v(19.97, -11.22) * mm, "mid": v(19.82, -11.58) * mm, "end": v(19.47, -11.72) * mm});
            skCircle(sketch, "E461.0.MirrorC", {"center": v(9.97, -14.22) * mm, "radius": 2.15 * mm});
            skCircle(sketch, "E462.0.MirrorC", {"center": v(-10.03, -14.22) * mm, "radius": 2.15 * mm});
            skArc(sketch, "E463.0.MirrorCS", {"start": v(-6, -17.16) * mm, "mid": v(-6.32, -16.68) * mm, "end": v(-6.43, -16.1) * mm});
            skLineSegment(sketch, "E464.0.MirrorCS", {"start": v(-6, -17.16) * mm, "end": v(-1.17, -21.98) * mm});
            skArc(sketch, "E465.0.MirrorCS", {"start": v(-0.11, -22.42) * mm, "mid": v(-0.68, -22.3) * mm, "end": v(-1.17, -21.98) * mm});
            skLineSegment(sketch, "E466.0.MirrorCS", {"start": v(0.05, -22.42) * mm, "end": v(-0.11, -22.42) * mm});
            skArc(sketch, "E467.0.MirrorCS", {"start": v(1.1, -21.98) * mm, "mid": v(0.62, -22.3) * mm, "end": v(0.05, -22.42) * mm});
            skLineSegment(sketch, "E468.0.MirrorCS", {"start": v(1.1, -21.98) * mm, "end": v(5.93, -17.16) * mm});
            skArc(sketch, "E469.0.MirrorCS", {"start": v(6.37, -16.1) * mm, "mid": v(6.25, -16.68) * mm, "end": v(5.93, -17.16) * mm});
            skArc(sketch, "E470.0.MirrorCS", {"start": v(11.85, -10.62) * mm, "mid": v(12.42, -10.5) * mm, "end": v(12.9, -10.18) * mm});
            skLineSegment(sketch, "E471.0.MirrorCS", {"start": v(11.85, -10.62) * mm, "end": v(8.09, -10.62) * mm});
            skLineSegment(sketch, "E472.0.MirrorCS", {"start": v(6.37, -16.1) * mm, "end": v(6.37, -12.34) * mm});
            skLineSegment(sketch, "E473.0.MirrorCS", {"start": v(-6.43, -16.1) * mm, "end": v(-6.43, -12.34) * mm});
            skLineSegment(sketch, "E474.0.MirrorCS", {"start": v(-11.91, -10.62) * mm, "end": v(-8.15, -10.62) * mm});
            skArc(sketch, "E475.0.MirrorCS", {"start": v(-11.91, -10.62) * mm, "mid": v(-12.48, -10.5) * mm, "end": v(-12.97, -10.18) * mm});
            skLineSegment(sketch, "E476.0.MirrorCS", {"start": v(-17.8, -3.08) * mm, "end": v(-12.97, 1.74) * mm});
            skArc(sketch, "E477.0.MirrorCS", {"start": v(-18.23, -4.14) * mm, "mid": v(-18.12, -3.57) * mm, "end": v(-17.8, -3.08) * mm});
            skLineSegment(sketch, "E478.0.MirrorCS", {"start": v(-18.23, -4.3) * mm, "end": v(-18.23, -4.14) * mm});
            skArc(sketch, "E479.0.MirrorCS", {"start": v(-17.8, -5.36) * mm, "mid": v(-18.12, -4.88) * mm, "end": v(-18.23, -4.3) * mm});
            skLineSegment(sketch, "E480.0.MirrorCS", {"start": v(-17.8, -5.36) * mm, "end": v(-12.97, -10.18) * mm});
            skLineSegment(sketch, "E481", {"start": v(-0.03, -4.22) * mm, "end": v(18.47, 14.28) * mm, "construction": true});
            skLineSegment(sketch, "E482.0.MirrorCS", {"start": v(17.73, -3.08) * mm, "end": v(12.9, 1.74) * mm});
            skArc(sketch, "E483.0.MirrorCS", {"start": v(17.73, -3.08) * mm, "mid": v(18.05, -3.57) * mm, "end": v(18.17, -4.14) * mm});
            skLineSegment(sketch, "E484.0.MirrorCS", {"start": v(18.17, -4.14) * mm, "end": v(18.17, -4.3) * mm});
            skArc(sketch, "E485.0.MirrorCS", {"start": v(18.17, -4.3) * mm, "mid": v(18.05, -4.88) * mm, "end": v(17.73, -5.36) * mm});
            skLineSegment(sketch, "E486.0.MirrorCS", {"start": v(17.73, -5.36) * mm, "end": v(12.9, -10.18) * mm});
            skLineSegment(sketch, "E487", {"start": v(-8.15, 2.18) * mm, "end": v(-6.43, 3.9) * mm});
            skLineSegment(sketch, "E488", {"start": v(6.37, 3.9) * mm, "end": v(8.09, 2.18) * mm});
            skLineSegment(sketch, "E489", {"start": v(-6.43, -12.34) * mm, "end": v(-8.15, -10.62) * mm});
            skLineSegment(sketch, "E490", {"start": v(8.09, -10.62) * mm, "end": v(6.37, -12.34) * mm});
            skLineSegment(sketch, "E491", {"start": v(-20.03, 2.78) * mm, "end": v(-20.03, -11.22) * mm});
            skLineSegment(sketch, "E492", {"start": v(19.97, 2.78) * mm, "end": v(19.97, -11.22) * mm});
            skSolve(sketch);
        }
        {
            var Q0;
            Q0 = qSketchRegion(id + "F2", true);
            extrude(context, id + "F5", {"entities" : qUnion([Q0]), "depth" : 500 * mm});
        }
        {
            var Q0;
            Q0 = qSketchRegion(id + "F3", true);
            extrude(context, id + "F6", {"entities" : qUnion([Q0]), "depth" : 500 * mm});
        }
        {
            var Q0;
            Q0 = qSketchRegion(id + "F0", true);
            extrude(context, id + "F7", {"entities" : qUnion([Q0]), "depth" : 580 * mm});
        }
        {
            var Q0;
            Q0 = qSketchRegion(id + "F4", true);
            extrude(context, id + "F8", {"entities" : qUnion([Q0]), "depth" : 580 * mm});
        }
        {
            var Q0;
            Q0 = qSketchRegion(id + "F1", true);
            extrude(context, id + "F9", {"entities" : qUnion([Q0]), "depth" : 500 * mm});
        }
        {
            var Q0;
            Q0 = qSketchRegion(id + "F1", true);
            extrude(context, id + "F10", {"entities" : qUnion([Q0]), "depth" : 580 * mm});
        }
        {
            var Q0;
            Q0 = qSketchRegion(id + "F2", true);
            extrude(context, id + "F11", {"entities" : qUnion([Q0]), "depth" : 480 * mm});
        }
        {
            var Q0;
            Q0 = qSketchRegion(id + "F3", true);
            extrude(context, id + "F12", {"entities" : qUnion([Q0]), "depth" : 460 * mm});
        }
        {
            var Q0;
            Q0 = qSketchRegion(id + "F1", true);
            extrude(context, id + "F13", {"entities" : qUnion([Q0]), "depth" : 460 * mm});
        }
        {
            var Q0;
            Q0 = qSketchRegion(id + "F1", true);
            extrude(context, id + "F14", {"entities" : qUnion([Q0]), "depth" : 480 * mm});
        }
    });
